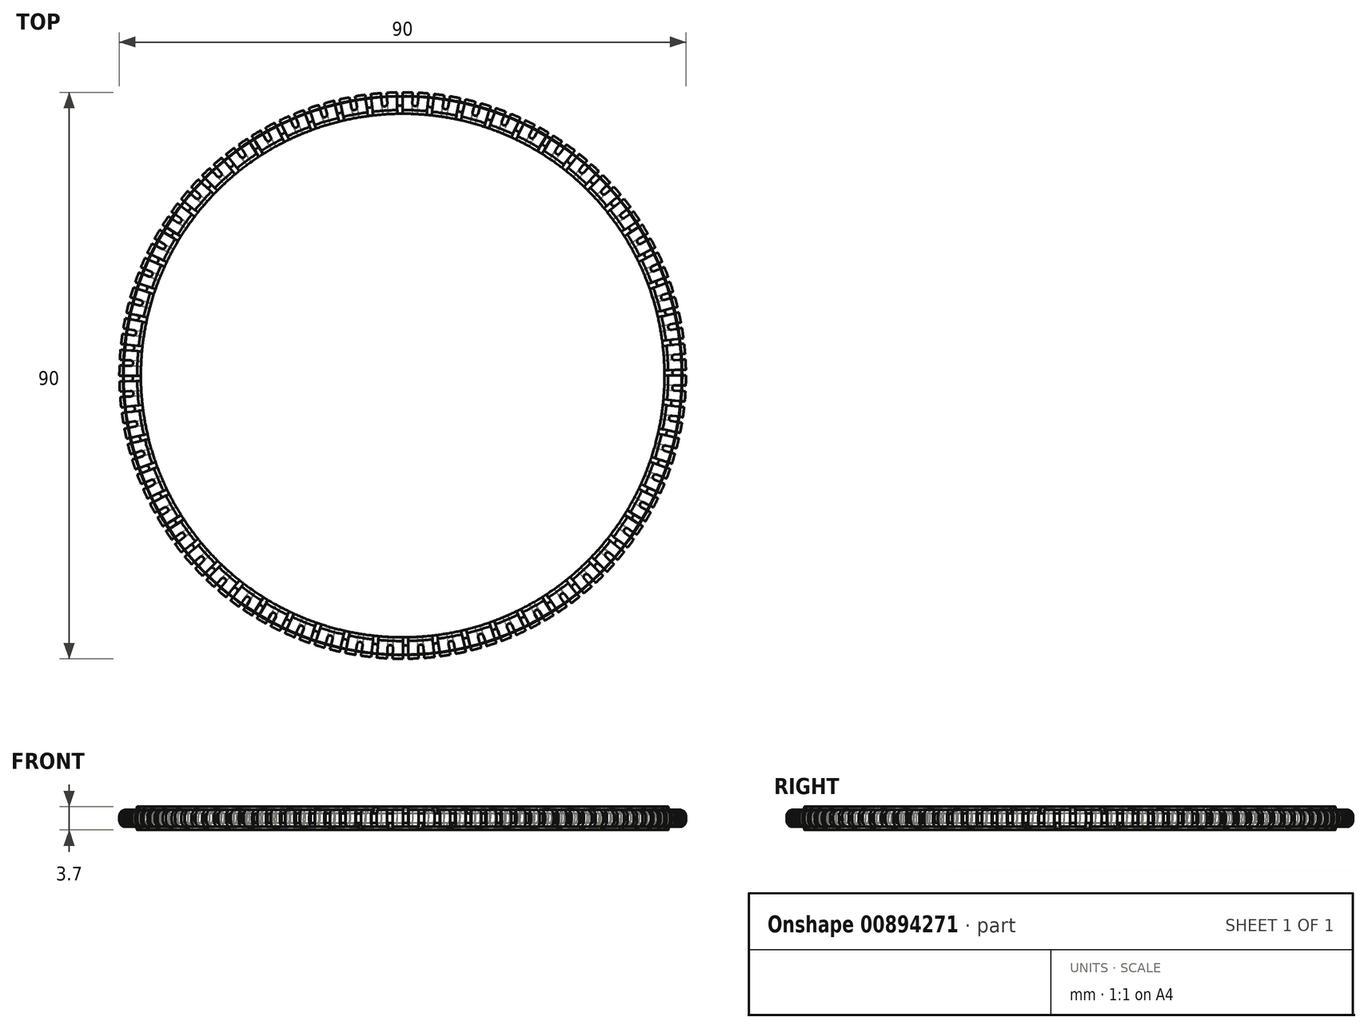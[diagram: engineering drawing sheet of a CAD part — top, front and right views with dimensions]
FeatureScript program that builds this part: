
annotation { "Feature Type Name" : "Feature", "Feature Type Description" : "" }
export const myFeature = defineFeature(function(context is Context, id is Id, definition is map)
    precondition{}
    {
        {
            var Q0;
            Q0=qCreatedBy(makeId("Right.planeOp"),FACE);
            var sketch = newSketch(context, id + "F0", { "sketchPlane" : qUnion([Q0])});
            skLineSegment(sketch, "E0", {"start": v(41.6, -1.73) * mm, "end": v(41.69, -1.3) * mm});
            skLineSegment(sketch, "E1", {"start": v(42.37, -0.75) * mm, "end": v(44, -0.75) * mm});
            skLineSegment(sketch, "E2", {"start": v(44.4, -0.35) * mm, "end": v(44.4, 0.35) * mm});
            skLineSegment(sketch, "E3", {"start": v(44, 0.75) * mm, "end": v(42.37, 0.75) * mm});
            skLineSegment(sketch, "E4", {"start": v(41.69, 1.3) * mm, "end": v(41.6, 1.73) * mm});
            skLineSegment(sketch, "E5", {"start": v(41.6, 1.73) * mm, "end": v(42.19, 1.85) * mm});
            skLineSegment(sketch, "E6", {"start": v(42.19, 1.85) * mm, "end": v(42.28, 1.43) * mm});
            skLineSegment(sketch, "E7", {"start": v(42.37, 1.35) * mm, "end": v(44, 1.35) * mm});
            skLineSegment(sketch, "E8", {"start": v(45, 0.35) * mm, "end": v(45, -0.35) * mm});
            skLineSegment(sketch, "E9", {"start": v(44, -1.35) * mm, "end": v(42.37, -1.35) * mm});
            skLineSegment(sketch, "E10", {"start": v(42.28, -1.43) * mm, "end": v(42.19, -1.85) * mm});
            skLineSegment(sketch, "E11", {"start": v(42.19, -1.85) * mm, "end": v(41.6, -1.73) * mm});
            skLineSegment(sketch, "E12", {"start": v(45, 0) * mm, "end": v(0, 0) * mm, "construction": true});
            skPoint(sketch, "E13.visualSharp", {"position": v(41.8, 0.75) * mm});
            skArc(sketch, "E13.filletArc", {"start": v(41.69, 1.3) * mm, "mid": v(41.93, 0.9) * mm, "end": v(42.37, 0.75) * mm});
            skPoint(sketch, "E14.visualSharp", {"position": v(42.3, 1.35) * mm});
            skArc(sketch, "E14.filletArc", {"start": v(42.28, 1.43) * mm, "mid": v(42.31, 1.37) * mm, "end": v(42.37, 1.35) * mm});
            skPoint(sketch, "E15.visualSharp", {"position": v(45, 1.35) * mm});
            skArc(sketch, "E15.filletArc", {"start": v(45, 0.35) * mm, "mid": v(44.7, 1.06) * mm, "end": v(44, 1.35) * mm});
            skPoint(sketch, "E16.visualSharp", {"position": v(45, -1.35) * mm});
            skArc(sketch, "E16.filletArc", {"start": v(44, -1.35) * mm, "mid": v(44.7, -1.06) * mm, "end": v(45, -0.35) * mm});
            skPoint(sketch, "E17.visualSharp", {"position": v(44.4, 0.75) * mm});
            skArc(sketch, "E17.filletArc", {"start": v(44.4, 0.35) * mm, "mid": v(44.28, 0.63) * mm, "end": v(44, 0.75) * mm});
            skPoint(sketch, "E18.visualSharp", {"position": v(44.4, -0.75) * mm});
            skArc(sketch, "E18.filletArc", {"start": v(44, -0.75) * mm, "mid": v(44.28, -0.63) * mm, "end": v(44.4, -0.35) * mm});
            skPoint(sketch, "E19.visualSharp", {"position": v(41.8, -0.75) * mm});
            skArc(sketch, "E19.filletArc", {"start": v(42.37, -0.75) * mm, "mid": v(41.93, -0.9) * mm, "end": v(41.69, -1.3) * mm});
            skPoint(sketch, "E20.visualSharp", {"position": v(42.3, -1.35) * mm});
            skArc(sketch, "E20.filletArc", {"start": v(42.37, -1.35) * mm, "mid": v(42.31, -1.37) * mm, "end": v(42.28, -1.43) * mm});
            skLineSegment(sketch, "E21", {"start": v(0, 0) * mm, "end": v(0, 20) * mm, "construction": true});
            skSolve(sketch);
        }
        {
            var Q0;
            Q0=makeQuery(id+"F0.imprint","IMPRINT",FACE,{"disambiguationData":[TD([[makeQuery(id+"F0.imprint","IMPRINT",EDGE,{"derivedFrom":sQuery(id+"F0.wireOp",EDGE,"E0")}),-1.0]])]});
            var Q1;
            Q1=sQuery(id+"F0.wireOp",EDGE,"E21");
            revolve(context, id + "F1", {"surfaceOperationType" : NewSurfaceOperationType.NEW, "entities" : qUnion([Q0]), "axis" : qUnion([Q1]), "revolveType" : RevolveType.FULL});
        }
        {
            var Q0;
            Q0=qCreatedBy(makeId("Top.planeOp"),FACE);
            var sketch = newSketch(context, id + "F2", { "sketchPlane" : qUnion([Q0])});
            skLineSegment(sketch, "E22", {"start": v(0, 0) * mm, "end": v(1.6, 44.97) * mm});
            skLineSegment(sketch, "E23", {"start": v(0, 0) * mm, "end": v(2.5, 44.93) * mm});
            skLineSegment(sketch, "E24", {"start": v(1.6, 44.97) * mm, "end": v(2.5, 44.93) * mm});
            skLineSegment(sketch, "E25", {"start": v(0, 0) * mm, "end": v(0, 45) * mm, "construction": true});
            skLineSegment(sketch, "E26.1.0", {"start": v(0, 0) * mm, "end": v(-2.55, 44.93) * mm});
            skLineSegment(sketch, "E26.1.1", {"start": v(0, 0) * mm, "end": v(-3.45, 44.87) * mm});
            skLineSegment(sketch, "E26.1.3", {"start": v(-3.45, 44.87) * mm, "end": v(-2.55, 44.93) * mm});
            skLineSegment(sketch, "E26.2.0", {"start": v(0, 0) * mm, "end": v(-7.56, 44.36) * mm});
            skLineSegment(sketch, "E26.2.1", {"start": v(0, 0) * mm, "end": v(-8.45, 44.2) * mm});
            skLineSegment(sketch, "E26.2.3", {"start": v(-8.45, 44.2) * mm, "end": v(-7.56, 44.36) * mm});
            skLineSegment(sketch, "E26.3.0", {"start": v(0, 0) * mm, "end": v(-12.48, 43.24) * mm});
            skLineSegment(sketch, "E26.3.1", {"start": v(0, 0) * mm, "end": v(-13.34, 42.98) * mm});
            skLineSegment(sketch, "E26.3.3", {"start": v(-13.34, 42.98) * mm, "end": v(-12.48, 43.24) * mm});
            skLineSegment(sketch, "E26.4.0", {"start": v(0, 0) * mm, "end": v(-17.24, 41.57) * mm});
            skLineSegment(sketch, "E26.4.1", {"start": v(0, 0) * mm, "end": v(-18.07, 41.21) * mm});
            skLineSegment(sketch, "E26.4.3", {"start": v(-18.07, 41.21) * mm, "end": v(-17.24, 41.57) * mm});
            skLineSegment(sketch, "E26.5.0", {"start": v(0, 0) * mm, "end": v(-21.79, 39.38) * mm});
            skLineSegment(sketch, "E26.5.1", {"start": v(0, 0) * mm, "end": v(-22.57, 38.93) * mm});
            skLineSegment(sketch, "E26.5.3", {"start": v(-22.57, 38.93) * mm, "end": v(-21.79, 39.38) * mm});
            skLineSegment(sketch, "E26.6.0", {"start": v(0, 0) * mm, "end": v(-26.06, 36.69) * mm});
            skLineSegment(sketch, "E26.6.1", {"start": v(0, 0) * mm, "end": v(-26.79, 36.16) * mm});
            skLineSegment(sketch, "E26.6.3", {"start": v(-26.79, 36.16) * mm, "end": v(-26.06, 36.69) * mm});
            skLineSegment(sketch, "E26.7.0", {"start": v(0, 0) * mm, "end": v(-30, 33.54) * mm});
            skLineSegment(sketch, "E26.7.1", {"start": v(0, 0) * mm, "end": v(-30.67, 32.93) * mm});
            skLineSegment(sketch, "E26.7.3", {"start": v(-30.67, 32.93) * mm, "end": v(-30, 33.54) * mm});
            skLineSegment(sketch, "E26.8.0", {"start": v(0, 0) * mm, "end": v(-33.57, 29.97) * mm});
            skLineSegment(sketch, "E26.8.1", {"start": v(0, 0) * mm, "end": v(-34.16, 29.3) * mm});
            skLineSegment(sketch, "E26.8.3", {"start": v(-34.16, 29.3) * mm, "end": v(-33.57, 29.97) * mm});
            skLineSegment(sketch, "E26.9.0", {"start": v(0, 0) * mm, "end": v(-36.72, 26.02) * mm});
            skLineSegment(sketch, "E26.9.1", {"start": v(0, 0) * mm, "end": v(-37.23, 25.28) * mm});
            skLineSegment(sketch, "E26.9.3", {"start": v(-37.23, 25.28) * mm, "end": v(-36.72, 26.02) * mm});
            skLineSegment(sketch, "E26.10.0", {"start": v(0, 0) * mm, "end": v(-39.4, 21.75) * mm});
            skLineSegment(sketch, "E26.10.1", {"start": v(0, 0) * mm, "end": v(-39.83, 20.95) * mm});
            skLineSegment(sketch, "E26.10.3", {"start": v(-39.83, 20.95) * mm, "end": v(-39.4, 21.75) * mm});
            skLineSegment(sketch, "E26.11.0", {"start": v(0, 0) * mm, "end": v(-41.59, 17.2) * mm});
            skLineSegment(sketch, "E26.11.1", {"start": v(0, 0) * mm, "end": v(-41.92, 16.36) * mm});
            skLineSegment(sketch, "E26.11.3", {"start": v(-41.92, 16.36) * mm, "end": v(-41.59, 17.2) * mm});
            skLineSegment(sketch, "E26.12.0", {"start": v(0, 0) * mm, "end": v(-43.25, 12.43) * mm});
            skLineSegment(sketch, "E26.12.1", {"start": v(0, 0) * mm, "end": v(-43.5, 11.57) * mm});
            skLineSegment(sketch, "E26.12.3", {"start": v(-43.5, 11.57) * mm, "end": v(-43.25, 12.43) * mm});
            skLineSegment(sketch, "E26.13.0", {"start": v(0, 0) * mm, "end": v(-44.37, 7.51) * mm});
            skLineSegment(sketch, "E26.13.1", {"start": v(0, 0) * mm, "end": v(-44.51, 6.63) * mm});
            skLineSegment(sketch, "E26.13.3", {"start": v(-44.51, 6.63) * mm, "end": v(-44.37, 7.51) * mm});
            skLineSegment(sketch, "E26.14.0", {"start": v(0, 0) * mm, "end": v(-44.93, 2.5) * mm});
            skLineSegment(sketch, "E26.14.1", {"start": v(0, 0) * mm, "end": v(-44.97, 1.6) * mm});
            skLineSegment(sketch, "E26.14.3", {"start": v(-44.97, 1.6) * mm, "end": v(-44.93, 2.5) * mm});
            skLineSegment(sketch, "E26.15.0", {"start": v(0, 0) * mm, "end": v(-44.93, -2.55) * mm});
            skLineSegment(sketch, "E26.15.1", {"start": v(0, 0) * mm, "end": v(-44.87, -3.45) * mm});
            skLineSegment(sketch, "E26.15.3", {"start": v(-44.87, -3.45) * mm, "end": v(-44.93, -2.55) * mm});
            skLineSegment(sketch, "E26.16.0", {"start": v(0, 0) * mm, "end": v(-44.36, -7.56) * mm});
            skLineSegment(sketch, "E26.16.1", {"start": v(0, 0) * mm, "end": v(-44.2, -8.45) * mm});
            skLineSegment(sketch, "E26.16.3", {"start": v(-44.2, -8.45) * mm, "end": v(-44.36, -7.56) * mm});
            skLineSegment(sketch, "E26.17.0", {"start": v(0, 0) * mm, "end": v(-43.24, -12.48) * mm});
            skLineSegment(sketch, "E26.17.1", {"start": v(0, 0) * mm, "end": v(-42.98, -13.34) * mm});
            skLineSegment(sketch, "E26.17.3", {"start": v(-42.98, -13.34) * mm, "end": v(-43.24, -12.48) * mm});
            skLineSegment(sketch, "E26.18.0", {"start": v(0, 0) * mm, "end": v(-41.57, -17.24) * mm});
            skLineSegment(sketch, "E26.18.1", {"start": v(0, 0) * mm, "end": v(-41.21, -18.07) * mm});
            skLineSegment(sketch, "E26.18.3", {"start": v(-41.21, -18.07) * mm, "end": v(-41.57, -17.24) * mm});
            skLineSegment(sketch, "E26.19.0", {"start": v(0, 0) * mm, "end": v(-39.38, -21.79) * mm});
            skLineSegment(sketch, "E26.19.1", {"start": v(0, 0) * mm, "end": v(-38.93, -22.57) * mm});
            skLineSegment(sketch, "E26.19.3", {"start": v(-38.93, -22.57) * mm, "end": v(-39.38, -21.79) * mm});
            skLineSegment(sketch, "E26.20.0", {"start": v(0, 0) * mm, "end": v(-36.69, -26.06) * mm});
            skLineSegment(sketch, "E26.20.1", {"start": v(0, 0) * mm, "end": v(-36.16, -26.79) * mm});
            skLineSegment(sketch, "E26.20.3", {"start": v(-36.16, -26.79) * mm, "end": v(-36.69, -26.06) * mm});
            skLineSegment(sketch, "E26.21.0", {"start": v(0, 0) * mm, "end": v(-33.54, -30) * mm});
            skLineSegment(sketch, "E26.21.1", {"start": v(0, 0) * mm, "end": v(-32.93, -30.67) * mm});
            skLineSegment(sketch, "E26.21.3", {"start": v(-32.93, -30.67) * mm, "end": v(-33.54, -30) * mm});
            skLineSegment(sketch, "E26.22.0", {"start": v(0, 0) * mm, "end": v(-29.97, -33.57) * mm});
            skLineSegment(sketch, "E26.22.1", {"start": v(0, 0) * mm, "end": v(-29.3, -34.16) * mm});
            skLineSegment(sketch, "E26.22.3", {"start": v(-29.3, -34.16) * mm, "end": v(-29.97, -33.57) * mm});
            skLineSegment(sketch, "E26.23.0", {"start": v(0, 0) * mm, "end": v(-26.02, -36.72) * mm});
            skLineSegment(sketch, "E26.23.1", {"start": v(0, 0) * mm, "end": v(-25.28, -37.23) * mm});
            skLineSegment(sketch, "E26.23.3", {"start": v(-25.28, -37.23) * mm, "end": v(-26.02, -36.72) * mm});
            skLineSegment(sketch, "E26.24.0", {"start": v(0, 0) * mm, "end": v(-21.75, -39.4) * mm});
            skLineSegment(sketch, "E26.24.1", {"start": v(0, 0) * mm, "end": v(-20.95, -39.83) * mm});
            skLineSegment(sketch, "E26.24.3", {"start": v(-20.95, -39.83) * mm, "end": v(-21.75, -39.4) * mm});
            skLineSegment(sketch, "E26.25.0", {"start": v(0, 0) * mm, "end": v(-17.2, -41.59) * mm});
            skLineSegment(sketch, "E26.25.1", {"start": v(0, 0) * mm, "end": v(-16.36, -41.92) * mm});
            skLineSegment(sketch, "E26.25.3", {"start": v(-16.36, -41.92) * mm, "end": v(-17.2, -41.59) * mm});
            skLineSegment(sketch, "E26.26.0", {"start": v(0, 0) * mm, "end": v(-12.43, -43.25) * mm});
            skLineSegment(sketch, "E26.26.1", {"start": v(0, 0) * mm, "end": v(-11.57, -43.5) * mm});
            skLineSegment(sketch, "E26.26.3", {"start": v(-11.57, -43.5) * mm, "end": v(-12.43, -43.25) * mm});
            skLineSegment(sketch, "E26.27.0", {"start": v(0, 0) * mm, "end": v(-7.51, -44.37) * mm});
            skLineSegment(sketch, "E26.27.1", {"start": v(0, 0) * mm, "end": v(-6.63, -44.51) * mm});
            skLineSegment(sketch, "E26.27.3", {"start": v(-6.63, -44.51) * mm, "end": v(-7.51, -44.37) * mm});
            skLineSegment(sketch, "E26.28.0", {"start": v(0, 0) * mm, "end": v(-2.5, -44.93) * mm});
            skLineSegment(sketch, "E26.28.1", {"start": v(0, 0) * mm, "end": v(-1.6, -44.97) * mm});
            skLineSegment(sketch, "E26.28.3", {"start": v(-1.6, -44.97) * mm, "end": v(-2.5, -44.93) * mm});
            skLineSegment(sketch, "E26.29.0", {"start": v(0, 0) * mm, "end": v(2.55, -44.93) * mm});
            skLineSegment(sketch, "E26.29.1", {"start": v(0, 0) * mm, "end": v(3.45, -44.87) * mm});
            skLineSegment(sketch, "E26.29.3", {"start": v(3.45, -44.87) * mm, "end": v(2.55, -44.93) * mm});
            skLineSegment(sketch, "E26.30.0", {"start": v(0, 0) * mm, "end": v(7.56, -44.36) * mm});
            skLineSegment(sketch, "E26.30.1", {"start": v(0, 0) * mm, "end": v(8.45, -44.2) * mm});
            skLineSegment(sketch, "E26.30.3", {"start": v(8.45, -44.2) * mm, "end": v(7.56, -44.36) * mm});
            skLineSegment(sketch, "E26.31.0", {"start": v(0, 0) * mm, "end": v(12.48, -43.24) * mm});
            skLineSegment(sketch, "E26.31.1", {"start": v(0, 0) * mm, "end": v(13.34, -42.98) * mm});
            skLineSegment(sketch, "E26.31.3", {"start": v(13.34, -42.98) * mm, "end": v(12.48, -43.24) * mm});
            skLineSegment(sketch, "E26.32.0", {"start": v(0, 0) * mm, "end": v(17.24, -41.57) * mm});
            skLineSegment(sketch, "E26.32.1", {"start": v(0, 0) * mm, "end": v(18.07, -41.21) * mm});
            skLineSegment(sketch, "E26.32.3", {"start": v(18.07, -41.21) * mm, "end": v(17.24, -41.57) * mm});
            skLineSegment(sketch, "E26.33.0", {"start": v(0, 0) * mm, "end": v(21.79, -39.38) * mm});
            skLineSegment(sketch, "E26.33.1", {"start": v(0, 0) * mm, "end": v(22.57, -38.93) * mm});
            skLineSegment(sketch, "E26.33.3", {"start": v(22.57, -38.93) * mm, "end": v(21.79, -39.38) * mm});
            skLineSegment(sketch, "E26.34.0", {"start": v(0, 0) * mm, "end": v(26.06, -36.69) * mm});
            skLineSegment(sketch, "E26.34.1", {"start": v(0, 0) * mm, "end": v(26.79, -36.16) * mm});
            skLineSegment(sketch, "E26.34.3", {"start": v(26.79, -36.16) * mm, "end": v(26.06, -36.69) * mm});
            skLineSegment(sketch, "E26.35.0", {"start": v(0, 0) * mm, "end": v(30, -33.54) * mm});
            skLineSegment(sketch, "E26.35.1", {"start": v(0, 0) * mm, "end": v(30.67, -32.93) * mm});
            skLineSegment(sketch, "E26.35.3", {"start": v(30.67, -32.93) * mm, "end": v(30, -33.54) * mm});
            skLineSegment(sketch, "E26.36.0", {"start": v(0, 0) * mm, "end": v(33.57, -29.97) * mm});
            skLineSegment(sketch, "E26.36.1", {"start": v(0, 0) * mm, "end": v(34.16, -29.3) * mm});
            skLineSegment(sketch, "E26.36.3", {"start": v(34.16, -29.3) * mm, "end": v(33.57, -29.97) * mm});
            skLineSegment(sketch, "E26.37.0", {"start": v(0, 0) * mm, "end": v(36.72, -26.02) * mm});
            skLineSegment(sketch, "E26.37.1", {"start": v(0, 0) * mm, "end": v(37.23, -25.28) * mm});
            skLineSegment(sketch, "E26.37.3", {"start": v(37.23, -25.28) * mm, "end": v(36.72, -26.02) * mm});
            skLineSegment(sketch, "E26.38.0", {"start": v(0, 0) * mm, "end": v(39.4, -21.75) * mm});
            skLineSegment(sketch, "E26.38.1", {"start": v(0, 0) * mm, "end": v(39.83, -20.95) * mm});
            skLineSegment(sketch, "E26.38.3", {"start": v(39.83, -20.95) * mm, "end": v(39.4, -21.75) * mm});
            skLineSegment(sketch, "E26.39.0", {"start": v(0, 0) * mm, "end": v(41.59, -17.2) * mm});
            skLineSegment(sketch, "E26.39.1", {"start": v(0, 0) * mm, "end": v(41.92, -16.36) * mm});
            skLineSegment(sketch, "E26.39.3", {"start": v(41.92, -16.36) * mm, "end": v(41.59, -17.2) * mm});
            skLineSegment(sketch, "E26.40.0", {"start": v(0, 0) * mm, "end": v(43.25, -12.43) * mm});
            skLineSegment(sketch, "E26.40.1", {"start": v(0, 0) * mm, "end": v(43.5, -11.57) * mm});
            skLineSegment(sketch, "E26.40.3", {"start": v(43.5, -11.57) * mm, "end": v(43.25, -12.43) * mm});
            skLineSegment(sketch, "E26.41.0", {"start": v(0, 0) * mm, "end": v(44.37, -7.51) * mm});
            skLineSegment(sketch, "E26.41.1", {"start": v(0, 0) * mm, "end": v(44.51, -6.63) * mm});
            skLineSegment(sketch, "E26.41.3", {"start": v(44.51, -6.63) * mm, "end": v(44.37, -7.51) * mm});
            skLineSegment(sketch, "E26.42.0", {"start": v(0, 0) * mm, "end": v(44.93, -2.5) * mm});
            skLineSegment(sketch, "E26.42.1", {"start": v(0, 0) * mm, "end": v(44.97, -1.6) * mm});
            skLineSegment(sketch, "E26.42.3", {"start": v(44.97, -1.6) * mm, "end": v(44.93, -2.5) * mm});
            skLineSegment(sketch, "E26.43.0", {"start": v(0, 0) * mm, "end": v(44.93, 2.55) * mm});
            skLineSegment(sketch, "E26.43.1", {"start": v(0, 0) * mm, "end": v(44.87, 3.45) * mm});
            skLineSegment(sketch, "E26.43.3", {"start": v(44.87, 3.45) * mm, "end": v(44.93, 2.55) * mm});
            skLineSegment(sketch, "E26.44.0", {"start": v(0, 0) * mm, "end": v(44.36, 7.56) * mm});
            skLineSegment(sketch, "E26.44.1", {"start": v(0, 0) * mm, "end": v(44.2, 8.45) * mm});
            skLineSegment(sketch, "E26.44.3", {"start": v(44.2, 8.45) * mm, "end": v(44.36, 7.56) * mm});
            skLineSegment(sketch, "E26.45.0", {"start": v(0, 0) * mm, "end": v(43.24, 12.48) * mm});
            skLineSegment(sketch, "E26.45.1", {"start": v(0, 0) * mm, "end": v(42.98, 13.34) * mm});
            skLineSegment(sketch, "E26.45.3", {"start": v(42.98, 13.34) * mm, "end": v(43.24, 12.48) * mm});
            skLineSegment(sketch, "E26.46.0", {"start": v(0, 0) * mm, "end": v(41.57, 17.24) * mm});
            skLineSegment(sketch, "E26.46.1", {"start": v(0, 0) * mm, "end": v(41.21, 18.07) * mm});
            skLineSegment(sketch, "E26.46.3", {"start": v(41.21, 18.07) * mm, "end": v(41.57, 17.24) * mm});
            skLineSegment(sketch, "E26.47.0", {"start": v(0, 0) * mm, "end": v(39.38, 21.79) * mm});
            skLineSegment(sketch, "E26.47.1", {"start": v(0, 0) * mm, "end": v(38.93, 22.57) * mm});
            skLineSegment(sketch, "E26.47.3", {"start": v(38.93, 22.57) * mm, "end": v(39.38, 21.79) * mm});
            skLineSegment(sketch, "E26.48.0", {"start": v(0, 0) * mm, "end": v(36.69, 26.06) * mm});
            skLineSegment(sketch, "E26.48.1", {"start": v(0, 0) * mm, "end": v(36.16, 26.79) * mm});
            skLineSegment(sketch, "E26.48.3", {"start": v(36.16, 26.79) * mm, "end": v(36.69, 26.06) * mm});
            skLineSegment(sketch, "E26.49.0", {"start": v(0, 0) * mm, "end": v(33.54, 30) * mm});
            skLineSegment(sketch, "E26.49.1", {"start": v(0, 0) * mm, "end": v(32.93, 30.67) * mm});
            skLineSegment(sketch, "E26.49.3", {"start": v(32.93, 30.67) * mm, "end": v(33.54, 30) * mm});
            skLineSegment(sketch, "E26.50.0", {"start": v(0, 0) * mm, "end": v(29.97, 33.57) * mm});
            skLineSegment(sketch, "E26.50.1", {"start": v(0, 0) * mm, "end": v(29.3, 34.16) * mm});
            skLineSegment(sketch, "E26.50.3", {"start": v(29.3, 34.16) * mm, "end": v(29.97, 33.57) * mm});
            skLineSegment(sketch, "E26.51.0", {"start": v(0, 0) * mm, "end": v(26.02, 36.72) * mm});
            skLineSegment(sketch, "E26.51.1", {"start": v(0, 0) * mm, "end": v(25.28, 37.23) * mm});
            skLineSegment(sketch, "E26.51.3", {"start": v(25.28, 37.23) * mm, "end": v(26.02, 36.72) * mm});
            skLineSegment(sketch, "E26.52.0", {"start": v(0, 0) * mm, "end": v(21.75, 39.4) * mm});
            skLineSegment(sketch, "E26.52.1", {"start": v(0, 0) * mm, "end": v(20.95, 39.83) * mm});
            skLineSegment(sketch, "E26.52.3", {"start": v(20.95, 39.83) * mm, "end": v(21.75, 39.4) * mm});
            skLineSegment(sketch, "E26.53.0", {"start": v(0, 0) * mm, "end": v(17.2, 41.59) * mm});
            skLineSegment(sketch, "E26.53.1", {"start": v(0, 0) * mm, "end": v(16.36, 41.92) * mm});
            skLineSegment(sketch, "E26.53.3", {"start": v(16.36, 41.92) * mm, "end": v(17.2, 41.59) * mm});
            skLineSegment(sketch, "E26.54.0", {"start": v(0, 0) * mm, "end": v(12.43, 43.25) * mm});
            skLineSegment(sketch, "E26.54.1", {"start": v(0, 0) * mm, "end": v(11.57, 43.5) * mm});
            skLineSegment(sketch, "E26.54.3", {"start": v(11.57, 43.5) * mm, "end": v(12.43, 43.25) * mm});
            skLineSegment(sketch, "E26.55.0", {"start": v(0, 0) * mm, "end": v(7.51, 44.37) * mm});
            skLineSegment(sketch, "E26.55.1", {"start": v(0, 0) * mm, "end": v(6.63, 44.51) * mm});
            skLineSegment(sketch, "E26.55.3", {"start": v(6.63, 44.51) * mm, "end": v(7.51, 44.37) * mm});
            skPoint(sketch, "E26.center", {"position": v(0, 0) * mm});
            skLineSegment(sketch, "E27", {"start": v(0, 0) * mm, "end": v(3.96, 43.12) * mm, "construction": true});
            skLineSegment(sketch, "E28", {"start": v(0, 0) * mm, "end": v(4.83, 43.03) * mm, "construction": true});
            skLineSegment(sketch, "E29", {"start": v(3.96, 43.12) * mm, "end": v(4.83, 43.03) * mm, "construction": true});
            skLineSegment(sketch, "E30", {"start": v(3.96, 43.12) * mm, "end": v(4.12, 44.81) * mm});
            skLineSegment(sketch, "E31", {"start": v(4.83, 43.03) * mm, "end": v(5.01, 44.72) * mm});
            skLineSegment(sketch, "E32", {"start": v(4.12, 44.81) * mm, "end": v(5.01, 44.72) * mm});
            skArc(sketch, "E33", {"start": v(3.96, 43.12) * mm, "mid": v(4.35, 42.65) * mm, "end": v(4.83, 43.03) * mm});
            skLineSegment(sketch, "E34.1.0", {"start": v(-0.89, 43.3) * mm, "end": v(-0.92, 45) * mm});
            skLineSegment(sketch, "E34.1.1", {"start": v(-0.02, 43.3) * mm, "end": v(-0.02, 45) * mm});
            skLineSegment(sketch, "E34.1.2", {"start": v(-0.92, 45) * mm, "end": v(-0.02, 45) * mm});
            skArc(sketch, "E34.1.3", {"start": v(-0.89, 43.3) * mm, "mid": v(-0.45, 42.86) * mm, "end": v(-0.02, 43.3) * mm});
            skLineSegment(sketch, "E34.1.4", {"start": v(0, 0) * mm, "end": v(-5.04, 44.72) * mm, "construction": true});
            skLineSegment(sketch, "E34.2.0", {"start": v(-5.73, 42.92) * mm, "end": v(-5.96, 44.6) * mm});
            skLineSegment(sketch, "E34.2.1", {"start": v(-4.87, 43.03) * mm, "end": v(-5.06, 44.72) * mm});
            skLineSegment(sketch, "E34.2.2", {"start": v(-5.96, 44.6) * mm, "end": v(-5.06, 44.72) * mm});
            skArc(sketch, "E34.2.3", {"start": v(-5.73, 42.92) * mm, "mid": v(-5.25, 42.54) * mm, "end": v(-4.87, 43.03) * mm});
            skLineSegment(sketch, "E34.2.4", {"start": v(0, 0) * mm, "end": v(-10.01, 43.87) * mm, "construction": true});
            skLineSegment(sketch, "E34.3.0", {"start": v(-10.5, 42) * mm, "end": v(-10.91, 43.66) * mm});
            skLineSegment(sketch, "E34.3.1", {"start": v(-9.66, 42.21) * mm, "end": v(-10.04, 43.87) * mm});
            skLineSegment(sketch, "E34.3.2", {"start": v(-10.91, 43.66) * mm, "end": v(-10.04, 43.87) * mm});
            skArc(sketch, "E34.3.3", {"start": v(-10.5, 42) * mm, "mid": v(-9.98, 41.69) * mm, "end": v(-9.66, 42.21) * mm});
            skLineSegment(sketch, "E34.3.4", {"start": v(0, 0) * mm, "end": v(-14.86, 42.47) * mm, "construction": true});
            skLineSegment(sketch, "E34.4.0", {"start": v(-15.14, 40.57) * mm, "end": v(-15.73, 42.16) * mm});
            skLineSegment(sketch, "E34.4.1", {"start": v(-14.32, 40.86) * mm, "end": v(-14.89, 42.47) * mm});
            skLineSegment(sketch, "E34.4.2", {"start": v(-15.73, 42.16) * mm, "end": v(-14.89, 42.47) * mm});
            skArc(sketch, "E34.4.3", {"start": v(-15.14, 40.57) * mm, "mid": v(-14.58, 40.3) * mm, "end": v(-14.32, 40.86) * mm});
            skLineSegment(sketch, "E34.4.4", {"start": v(0, 0) * mm, "end": v(-19.52, 40.54) * mm, "construction": true});
            skLineSegment(sketch, "E34.5.0", {"start": v(-19.59, 38.62) * mm, "end": v(-20.35, 40.14) * mm});
            skLineSegment(sketch, "E34.5.1", {"start": v(-18.8, 39) * mm, "end": v(-19.55, 40.54) * mm});
            skLineSegment(sketch, "E34.5.2", {"start": v(-20.35, 40.14) * mm, "end": v(-19.55, 40.54) * mm});
            skArc(sketch, "E34.5.3", {"start": v(-19.59, 38.62) * mm, "mid": v(-19, 38.42) * mm, "end": v(-18.8, 39) * mm});
            skLineSegment(sketch, "E34.5.4", {"start": v(0, 0) * mm, "end": v(-23.94, 38.1) * mm, "construction": true});
            skLineSegment(sketch, "E34.6.0", {"start": v(-23.79, 36.18) * mm, "end": v(-24.72, 37.6) * mm});
            skLineSegment(sketch, "E34.6.1", {"start": v(-23.06, 36.65) * mm, "end": v(-23.96, 38.1) * mm});
            skLineSegment(sketch, "E34.6.2", {"start": v(-24.72, 37.6) * mm, "end": v(-23.96, 38.1) * mm});
            skArc(sketch, "E34.6.3", {"start": v(-23.79, 36.18) * mm, "mid": v(-23.19, 36.05) * mm, "end": v(-23.06, 36.65) * mm});
            skLineSegment(sketch, "E34.6.4", {"start": v(0, 0) * mm, "end": v(-28.06, 35.18) * mm, "construction": true});
            skLineSegment(sketch, "E34.7.0", {"start": v(-27.69, 33.3) * mm, "end": v(-28.78, 34.6) * mm});
            skLineSegment(sketch, "E34.7.1", {"start": v(-27.02, 33.84) * mm, "end": v(-28.08, 35.17) * mm});
            skLineSegment(sketch, "E34.7.2", {"start": v(-28.78, 34.6) * mm, "end": v(-28.08, 35.17) * mm});
            skArc(sketch, "E34.7.3", {"start": v(-27.69, 33.3) * mm, "mid": v(-27.08, 33.23) * mm, "end": v(-27.02, 33.84) * mm});
            skLineSegment(sketch, "E34.7.4", {"start": v(0, 0) * mm, "end": v(-31.82, 31.82) * mm, "construction": true});
            skLineSegment(sketch, "E34.8.0", {"start": v(-31.24, 29.98) * mm, "end": v(-32.47, 31.16) * mm});
            skLineSegment(sketch, "E34.8.1", {"start": v(-30.64, 30.6) * mm, "end": v(-31.84, 31.8) * mm});
            skLineSegment(sketch, "E34.8.2", {"start": v(-32.47, 31.16) * mm, "end": v(-31.84, 31.8) * mm});
            skArc(sketch, "E34.8.3", {"start": v(-31.24, 29.98) * mm, "mid": v(-30.63, 30) * mm, "end": v(-30.64, 30.6) * mm});
            skLineSegment(sketch, "E34.8.4", {"start": v(0, 0) * mm, "end": v(-35.18, 28.06) * mm, "construction": true});
            skLineSegment(sketch, "E34.9.0", {"start": v(-34.4, 26.3) * mm, "end": v(-35.75, 27.33) * mm});
            skLineSegment(sketch, "E34.9.1", {"start": v(-33.87, 26.98) * mm, "end": v(-35.2, 28.04) * mm});
            skLineSegment(sketch, "E34.9.2", {"start": v(-35.75, 27.33) * mm, "end": v(-35.2, 28.04) * mm});
            skArc(sketch, "E34.9.3", {"start": v(-34.4, 26.3) * mm, "mid": v(-33.8, 26.37) * mm, "end": v(-33.87, 26.98) * mm});
            skLineSegment(sketch, "E34.9.4", {"start": v(0, 0) * mm, "end": v(-38.1, 23.94) * mm, "construction": true});
            skLineSegment(sketch, "E34.10.0", {"start": v(-37.13, 22.28) * mm, "end": v(-38.59, 23.16) * mm});
            skLineSegment(sketch, "E34.10.1", {"start": v(-36.68, 23.02) * mm, "end": v(-38.12, 23.92) * mm});
            skLineSegment(sketch, "E34.10.2", {"start": v(-38.59, 23.16) * mm, "end": v(-38.12, 23.92) * mm});
            skArc(sketch, "E34.10.3", {"start": v(-37.13, 22.28) * mm, "mid": v(-36.53, 22.42) * mm, "end": v(-36.68, 23.02) * mm});
            skLineSegment(sketch, "E34.10.4", {"start": v(0, 0) * mm, "end": v(-40.54, 19.52) * mm, "construction": true});
            skLineSegment(sketch, "E34.11.0", {"start": v(-39.4, 17.98) * mm, "end": v(-40.94, 18.69) * mm});
            skLineSegment(sketch, "E34.11.1", {"start": v(-39.02, 18.77) * mm, "end": v(-40.56, 19.5) * mm});
            skLineSegment(sketch, "E34.11.2", {"start": v(-40.94, 18.69) * mm, "end": v(-40.56, 19.5) * mm});
            skArc(sketch, "E34.11.3", {"start": v(-39.4, 17.98) * mm, "mid": v(-38.82, 18.2) * mm, "end": v(-39.02, 18.77) * mm});
            skLineSegment(sketch, "E34.11.4", {"start": v(0, 0) * mm, "end": v(-42.47, 14.86) * mm, "construction": true});
            skLineSegment(sketch, "E34.12.0", {"start": v(-41.16, 13.46) * mm, "end": v(-42.77, 13.99) * mm});
            skLineSegment(sketch, "E34.12.1", {"start": v(-40.88, 14.28) * mm, "end": v(-42.48, 14.84) * mm});
            skLineSegment(sketch, "E34.12.2", {"start": v(-42.77, 13.99) * mm, "end": v(-42.48, 14.84) * mm});
            skArc(sketch, "E34.12.3", {"start": v(-41.16, 13.46) * mm, "mid": v(-40.6, 13.73) * mm, "end": v(-40.88, 14.28) * mm});
            skLineSegment(sketch, "E34.12.4", {"start": v(0, 0) * mm, "end": v(-43.87, 10.01) * mm, "construction": true});
            skLineSegment(sketch, "E34.13.0", {"start": v(-42.4, 8.77) * mm, "end": v(-44.07, 9.11) * mm});
            skLineSegment(sketch, "E34.13.1", {"start": v(-42.22, 9.61) * mm, "end": v(-43.88, 10) * mm});
            skLineSegment(sketch, "E34.13.2", {"start": v(-44.07, 9.11) * mm, "end": v(-43.88, 10) * mm});
            skArc(sketch, "E34.13.3", {"start": v(-42.4, 8.77) * mm, "mid": v(-41.9, 9.1) * mm, "end": v(-42.22, 9.61) * mm});
            skLineSegment(sketch, "E34.13.4", {"start": v(0, 0) * mm, "end": v(-44.72, 5.04) * mm, "construction": true});
            skLineSegment(sketch, "E34.14.0", {"start": v(-43.12, 3.96) * mm, "end": v(-44.81, 4.12) * mm});
            skLineSegment(sketch, "E34.14.1", {"start": v(-43.03, 4.83) * mm, "end": v(-44.72, 5.01) * mm});
            skLineSegment(sketch, "E34.14.2", {"start": v(-44.81, 4.12) * mm, "end": v(-44.72, 5.01) * mm});
            skArc(sketch, "E34.14.3", {"start": v(-43.12, 3.96) * mm, "mid": v(-42.65, 4.35) * mm, "end": v(-43.03, 4.83) * mm});
            skLineSegment(sketch, "E34.14.4", {"start": v(0, 0) * mm, "end": v(-45, 0) * mm, "construction": true});
            skLineSegment(sketch, "E34.15.0", {"start": v(-43.3, -0.89) * mm, "end": v(-45, -0.92) * mm});
            skLineSegment(sketch, "E34.15.1", {"start": v(-43.3, -0.02) * mm, "end": v(-45, -0.02) * mm});
            skLineSegment(sketch, "E34.15.2", {"start": v(-45, -0.92) * mm, "end": v(-45, -0.02) * mm});
            skArc(sketch, "E34.15.3", {"start": v(-43.3, -0.89) * mm, "mid": v(-42.86, -0.45) * mm, "end": v(-43.3, -0.02) * mm});
            skLineSegment(sketch, "E34.15.4", {"start": v(0, 0) * mm, "end": v(-44.72, -5.04) * mm, "construction": true});
            skLineSegment(sketch, "E34.16.0", {"start": v(-42.92, -5.73) * mm, "end": v(-44.6, -5.96) * mm});
            skLineSegment(sketch, "E34.16.1", {"start": v(-43.03, -4.87) * mm, "end": v(-44.72, -5.06) * mm});
            skLineSegment(sketch, "E34.16.2", {"start": v(-44.6, -5.96) * mm, "end": v(-44.72, -5.06) * mm});
            skArc(sketch, "E34.16.3", {"start": v(-42.92, -5.73) * mm, "mid": v(-42.54, -5.25) * mm, "end": v(-43.03, -4.87) * mm});
            skLineSegment(sketch, "E34.16.4", {"start": v(0, 0) * mm, "end": v(-43.87, -10.01) * mm, "construction": true});
            skLineSegment(sketch, "E34.17.0", {"start": v(-42, -10.5) * mm, "end": v(-43.66, -10.91) * mm});
            skLineSegment(sketch, "E34.17.1", {"start": v(-42.21, -9.66) * mm, "end": v(-43.87, -10.04) * mm});
            skLineSegment(sketch, "E34.17.2", {"start": v(-43.66, -10.91) * mm, "end": v(-43.87, -10.04) * mm});
            skArc(sketch, "E34.17.3", {"start": v(-42, -10.5) * mm, "mid": v(-41.69, -9.98) * mm, "end": v(-42.21, -9.66) * mm});
            skLineSegment(sketch, "E34.17.4", {"start": v(0, 0) * mm, "end": v(-42.47, -14.86) * mm, "construction": true});
            skLineSegment(sketch, "E34.18.0", {"start": v(-40.57, -15.14) * mm, "end": v(-42.16, -15.73) * mm});
            skLineSegment(sketch, "E34.18.1", {"start": v(-40.86, -14.32) * mm, "end": v(-42.47, -14.89) * mm});
            skLineSegment(sketch, "E34.18.2", {"start": v(-42.16, -15.73) * mm, "end": v(-42.47, -14.89) * mm});
            skArc(sketch, "E34.18.3", {"start": v(-40.57, -15.14) * mm, "mid": v(-40.3, -14.58) * mm, "end": v(-40.86, -14.32) * mm});
            skLineSegment(sketch, "E34.18.4", {"start": v(0, 0) * mm, "end": v(-40.54, -19.52) * mm, "construction": true});
            skLineSegment(sketch, "E34.19.0", {"start": v(-38.62, -19.59) * mm, "end": v(-40.14, -20.35) * mm});
            skLineSegment(sketch, "E34.19.1", {"start": v(-39, -18.8) * mm, "end": v(-40.54, -19.55) * mm});
            skLineSegment(sketch, "E34.19.2", {"start": v(-40.14, -20.35) * mm, "end": v(-40.54, -19.55) * mm});
            skArc(sketch, "E34.19.3", {"start": v(-38.62, -19.59) * mm, "mid": v(-38.42, -19) * mm, "end": v(-39, -18.8) * mm});
            skLineSegment(sketch, "E34.19.4", {"start": v(0, 0) * mm, "end": v(-38.1, -23.94) * mm, "construction": true});
            skLineSegment(sketch, "E34.20.0", {"start": v(-36.18, -23.79) * mm, "end": v(-37.6, -24.72) * mm});
            skLineSegment(sketch, "E34.20.1", {"start": v(-36.65, -23.06) * mm, "end": v(-38.1, -23.96) * mm});
            skLineSegment(sketch, "E34.20.2", {"start": v(-37.6, -24.72) * mm, "end": v(-38.1, -23.96) * mm});
            skArc(sketch, "E34.20.3", {"start": v(-36.18, -23.79) * mm, "mid": v(-36.05, -23.19) * mm, "end": v(-36.65, -23.06) * mm});
            skLineSegment(sketch, "E34.20.4", {"start": v(0, 0) * mm, "end": v(-35.18, -28.06) * mm, "construction": true});
            skLineSegment(sketch, "E34.21.0", {"start": v(-33.3, -27.69) * mm, "end": v(-34.6, -28.78) * mm});
            skLineSegment(sketch, "E34.21.1", {"start": v(-33.84, -27.02) * mm, "end": v(-35.17, -28.08) * mm});
            skLineSegment(sketch, "E34.21.2", {"start": v(-34.6, -28.78) * mm, "end": v(-35.17, -28.08) * mm});
            skArc(sketch, "E34.21.3", {"start": v(-33.3, -27.69) * mm, "mid": v(-33.23, -27.08) * mm, "end": v(-33.84, -27.02) * mm});
            skLineSegment(sketch, "E34.21.4", {"start": v(0, 0) * mm, "end": v(-31.82, -31.82) * mm, "construction": true});
            skLineSegment(sketch, "E34.22.0", {"start": v(-29.98, -31.24) * mm, "end": v(-31.16, -32.47) * mm});
            skLineSegment(sketch, "E34.22.1", {"start": v(-30.6, -30.64) * mm, "end": v(-31.8, -31.84) * mm});
            skLineSegment(sketch, "E34.22.2", {"start": v(-31.16, -32.47) * mm, "end": v(-31.8, -31.84) * mm});
            skArc(sketch, "E34.22.3", {"start": v(-29.98, -31.24) * mm, "mid": v(-30, -30.63) * mm, "end": v(-30.6, -30.64) * mm});
            skLineSegment(sketch, "E34.22.4", {"start": v(0, 0) * mm, "end": v(-28.06, -35.18) * mm, "construction": true});
            skLineSegment(sketch, "E34.23.0", {"start": v(-26.3, -34.4) * mm, "end": v(-27.33, -35.75) * mm});
            skLineSegment(sketch, "E34.23.1", {"start": v(-26.98, -33.87) * mm, "end": v(-28.04, -35.2) * mm});
            skLineSegment(sketch, "E34.23.2", {"start": v(-27.33, -35.75) * mm, "end": v(-28.04, -35.2) * mm});
            skArc(sketch, "E34.23.3", {"start": v(-26.3, -34.4) * mm, "mid": v(-26.37, -33.8) * mm, "end": v(-26.98, -33.87) * mm});
            skLineSegment(sketch, "E34.23.4", {"start": v(0, 0) * mm, "end": v(-23.94, -38.1) * mm, "construction": true});
            skLineSegment(sketch, "E34.24.0", {"start": v(-22.28, -37.13) * mm, "end": v(-23.16, -38.59) * mm});
            skLineSegment(sketch, "E34.24.1", {"start": v(-23.02, -36.68) * mm, "end": v(-23.92, -38.12) * mm});
            skLineSegment(sketch, "E34.24.2", {"start": v(-23.16, -38.59) * mm, "end": v(-23.92, -38.12) * mm});
            skArc(sketch, "E34.24.3", {"start": v(-22.28, -37.13) * mm, "mid": v(-22.42, -36.53) * mm, "end": v(-23.02, -36.68) * mm});
            skLineSegment(sketch, "E34.24.4", {"start": v(0, 0) * mm, "end": v(-19.52, -40.54) * mm, "construction": true});
            skLineSegment(sketch, "E34.25.0", {"start": v(-17.98, -39.4) * mm, "end": v(-18.69, -40.94) * mm});
            skLineSegment(sketch, "E34.25.1", {"start": v(-18.77, -39.02) * mm, "end": v(-19.5, -40.56) * mm});
            skLineSegment(sketch, "E34.25.2", {"start": v(-18.69, -40.94) * mm, "end": v(-19.5, -40.56) * mm});
            skArc(sketch, "E34.25.3", {"start": v(-17.98, -39.4) * mm, "mid": v(-18.2, -38.82) * mm, "end": v(-18.77, -39.02) * mm});
            skLineSegment(sketch, "E34.25.4", {"start": v(0, 0) * mm, "end": v(-14.86, -42.47) * mm, "construction": true});
            skLineSegment(sketch, "E34.26.0", {"start": v(-13.46, -41.16) * mm, "end": v(-13.99, -42.77) * mm});
            skLineSegment(sketch, "E34.26.1", {"start": v(-14.28, -40.88) * mm, "end": v(-14.84, -42.48) * mm});
            skLineSegment(sketch, "E34.26.2", {"start": v(-13.99, -42.77) * mm, "end": v(-14.84, -42.48) * mm});
            skArc(sketch, "E34.26.3", {"start": v(-13.46, -41.16) * mm, "mid": v(-13.73, -40.6) * mm, "end": v(-14.28, -40.88) * mm});
            skLineSegment(sketch, "E34.26.4", {"start": v(0, 0) * mm, "end": v(-10.01, -43.87) * mm, "construction": true});
            skLineSegment(sketch, "E34.27.0", {"start": v(-8.77, -42.4) * mm, "end": v(-9.11, -44.07) * mm});
            skLineSegment(sketch, "E34.27.1", {"start": v(-9.61, -42.22) * mm, "end": v(-10, -43.88) * mm});
            skLineSegment(sketch, "E34.27.2", {"start": v(-9.11, -44.07) * mm, "end": v(-10, -43.88) * mm});
            skArc(sketch, "E34.27.3", {"start": v(-8.77, -42.4) * mm, "mid": v(-9.1, -41.9) * mm, "end": v(-9.61, -42.22) * mm});
            skLineSegment(sketch, "E34.27.4", {"start": v(0, 0) * mm, "end": v(-5.04, -44.72) * mm, "construction": true});
            skLineSegment(sketch, "E34.28.0", {"start": v(-3.96, -43.12) * mm, "end": v(-4.12, -44.81) * mm});
            skLineSegment(sketch, "E34.28.1", {"start": v(-4.83, -43.03) * mm, "end": v(-5.01, -44.72) * mm});
            skLineSegment(sketch, "E34.28.2", {"start": v(-4.12, -44.81) * mm, "end": v(-5.01, -44.72) * mm});
            skArc(sketch, "E34.28.3", {"start": v(-3.96, -43.12) * mm, "mid": v(-4.35, -42.65) * mm, "end": v(-4.83, -43.03) * mm});
            skLineSegment(sketch, "E34.28.4", {"start": v(0, 0) * mm, "end": v(0, -45) * mm, "construction": true});
            skLineSegment(sketch, "E34.29.0", {"start": v(0.89, -43.3) * mm, "end": v(0.92, -45) * mm});
            skLineSegment(sketch, "E34.29.1", {"start": v(0.02, -43.3) * mm, "end": v(0.02, -45) * mm});
            skLineSegment(sketch, "E34.29.2", {"start": v(0.92, -45) * mm, "end": v(0.02, -45) * mm});
            skArc(sketch, "E34.29.3", {"start": v(0.89, -43.3) * mm, "mid": v(0.45, -42.86) * mm, "end": v(0.02, -43.3) * mm});
            skLineSegment(sketch, "E34.29.4", {"start": v(0, 0) * mm, "end": v(5.04, -44.72) * mm, "construction": true});
            skLineSegment(sketch, "E34.30.0", {"start": v(5.73, -42.92) * mm, "end": v(5.96, -44.6) * mm});
            skLineSegment(sketch, "E34.30.1", {"start": v(4.87, -43.03) * mm, "end": v(5.06, -44.72) * mm});
            skLineSegment(sketch, "E34.30.2", {"start": v(5.96, -44.6) * mm, "end": v(5.06, -44.72) * mm});
            skArc(sketch, "E34.30.3", {"start": v(5.73, -42.92) * mm, "mid": v(5.25, -42.54) * mm, "end": v(4.87, -43.03) * mm});
            skLineSegment(sketch, "E34.30.4", {"start": v(0, 0) * mm, "end": v(10.01, -43.87) * mm, "construction": true});
            skLineSegment(sketch, "E34.31.0", {"start": v(10.5, -42) * mm, "end": v(10.91, -43.66) * mm});
            skLineSegment(sketch, "E34.31.1", {"start": v(9.66, -42.21) * mm, "end": v(10.04, -43.87) * mm});
            skLineSegment(sketch, "E34.31.2", {"start": v(10.91, -43.66) * mm, "end": v(10.04, -43.87) * mm});
            skArc(sketch, "E34.31.3", {"start": v(10.5, -42) * mm, "mid": v(9.98, -41.69) * mm, "end": v(9.66, -42.21) * mm});
            skLineSegment(sketch, "E34.31.4", {"start": v(0, 0) * mm, "end": v(14.86, -42.47) * mm, "construction": true});
            skLineSegment(sketch, "E34.32.0", {"start": v(15.14, -40.57) * mm, "end": v(15.73, -42.16) * mm});
            skLineSegment(sketch, "E34.32.1", {"start": v(14.32, -40.86) * mm, "end": v(14.89, -42.47) * mm});
            skLineSegment(sketch, "E34.32.2", {"start": v(15.73, -42.16) * mm, "end": v(14.89, -42.47) * mm});
            skArc(sketch, "E34.32.3", {"start": v(15.14, -40.57) * mm, "mid": v(14.58, -40.3) * mm, "end": v(14.32, -40.86) * mm});
            skLineSegment(sketch, "E34.32.4", {"start": v(0, 0) * mm, "end": v(19.52, -40.54) * mm, "construction": true});
            skLineSegment(sketch, "E34.33.0", {"start": v(19.59, -38.62) * mm, "end": v(20.35, -40.14) * mm});
            skLineSegment(sketch, "E34.33.1", {"start": v(18.8, -39) * mm, "end": v(19.55, -40.54) * mm});
            skLineSegment(sketch, "E34.33.2", {"start": v(20.35, -40.14) * mm, "end": v(19.55, -40.54) * mm});
            skArc(sketch, "E34.33.3", {"start": v(19.59, -38.62) * mm, "mid": v(19, -38.42) * mm, "end": v(18.8, -39) * mm});
            skLineSegment(sketch, "E34.33.4", {"start": v(0, 0) * mm, "end": v(23.94, -38.1) * mm, "construction": true});
            skLineSegment(sketch, "E34.34.0", {"start": v(23.79, -36.18) * mm, "end": v(24.72, -37.6) * mm});
            skLineSegment(sketch, "E34.34.1", {"start": v(23.06, -36.65) * mm, "end": v(23.96, -38.1) * mm});
            skLineSegment(sketch, "E34.34.2", {"start": v(24.72, -37.6) * mm, "end": v(23.96, -38.1) * mm});
            skArc(sketch, "E34.34.3", {"start": v(23.79, -36.18) * mm, "mid": v(23.19, -36.05) * mm, "end": v(23.06, -36.65) * mm});
            skLineSegment(sketch, "E34.34.4", {"start": v(0, 0) * mm, "end": v(28.06, -35.18) * mm, "construction": true});
            skLineSegment(sketch, "E34.35.0", {"start": v(27.69, -33.3) * mm, "end": v(28.78, -34.6) * mm});
            skLineSegment(sketch, "E34.35.1", {"start": v(27.02, -33.84) * mm, "end": v(28.08, -35.17) * mm});
            skLineSegment(sketch, "E34.35.2", {"start": v(28.78, -34.6) * mm, "end": v(28.08, -35.17) * mm});
            skArc(sketch, "E34.35.3", {"start": v(27.69, -33.3) * mm, "mid": v(27.08, -33.23) * mm, "end": v(27.02, -33.84) * mm});
            skLineSegment(sketch, "E34.35.4", {"start": v(0, 0) * mm, "end": v(31.82, -31.82) * mm, "construction": true});
            skLineSegment(sketch, "E34.36.0", {"start": v(31.24, -29.98) * mm, "end": v(32.47, -31.16) * mm});
            skLineSegment(sketch, "E34.36.1", {"start": v(30.64, -30.6) * mm, "end": v(31.84, -31.8) * mm});
            skLineSegment(sketch, "E34.36.2", {"start": v(32.47, -31.16) * mm, "end": v(31.84, -31.8) * mm});
            skArc(sketch, "E34.36.3", {"start": v(31.24, -29.98) * mm, "mid": v(30.63, -30) * mm, "end": v(30.64, -30.6) * mm});
            skLineSegment(sketch, "E34.36.4", {"start": v(0, 0) * mm, "end": v(35.18, -28.06) * mm, "construction": true});
            skLineSegment(sketch, "E34.37.0", {"start": v(34.4, -26.3) * mm, "end": v(35.75, -27.33) * mm});
            skLineSegment(sketch, "E34.37.1", {"start": v(33.87, -26.98) * mm, "end": v(35.2, -28.04) * mm});
            skLineSegment(sketch, "E34.37.2", {"start": v(35.75, -27.33) * mm, "end": v(35.2, -28.04) * mm});
            skArc(sketch, "E34.37.3", {"start": v(34.4, -26.3) * mm, "mid": v(33.8, -26.37) * mm, "end": v(33.87, -26.98) * mm});
            skLineSegment(sketch, "E34.37.4", {"start": v(0, 0) * mm, "end": v(38.1, -23.94) * mm, "construction": true});
            skLineSegment(sketch, "E34.38.0", {"start": v(37.13, -22.28) * mm, "end": v(38.59, -23.16) * mm});
            skLineSegment(sketch, "E34.38.1", {"start": v(36.68, -23.02) * mm, "end": v(38.12, -23.92) * mm});
            skLineSegment(sketch, "E34.38.2", {"start": v(38.59, -23.16) * mm, "end": v(38.12, -23.92) * mm});
            skArc(sketch, "E34.38.3", {"start": v(37.13, -22.28) * mm, "mid": v(36.53, -22.42) * mm, "end": v(36.68, -23.02) * mm});
            skLineSegment(sketch, "E34.38.4", {"start": v(0, 0) * mm, "end": v(40.54, -19.52) * mm, "construction": true});
            skLineSegment(sketch, "E34.39.0", {"start": v(39.4, -17.98) * mm, "end": v(40.94, -18.69) * mm});
            skLineSegment(sketch, "E34.39.1", {"start": v(39.02, -18.77) * mm, "end": v(40.56, -19.5) * mm});
            skLineSegment(sketch, "E34.39.2", {"start": v(40.94, -18.69) * mm, "end": v(40.56, -19.5) * mm});
            skArc(sketch, "E34.39.3", {"start": v(39.4, -17.98) * mm, "mid": v(38.82, -18.2) * mm, "end": v(39.02, -18.77) * mm});
            skLineSegment(sketch, "E34.39.4", {"start": v(0, 0) * mm, "end": v(42.47, -14.86) * mm, "construction": true});
            skLineSegment(sketch, "E34.40.0", {"start": v(41.16, -13.46) * mm, "end": v(42.77, -13.99) * mm});
            skLineSegment(sketch, "E34.40.1", {"start": v(40.88, -14.28) * mm, "end": v(42.48, -14.84) * mm});
            skLineSegment(sketch, "E34.40.2", {"start": v(42.77, -13.99) * mm, "end": v(42.48, -14.84) * mm});
            skArc(sketch, "E34.40.3", {"start": v(41.16, -13.46) * mm, "mid": v(40.6, -13.73) * mm, "end": v(40.88, -14.28) * mm});
            skLineSegment(sketch, "E34.40.4", {"start": v(0, 0) * mm, "end": v(43.87, -10.01) * mm, "construction": true});
            skLineSegment(sketch, "E34.41.0", {"start": v(42.4, -8.77) * mm, "end": v(44.07, -9.11) * mm});
            skLineSegment(sketch, "E34.41.1", {"start": v(42.22, -9.61) * mm, "end": v(43.88, -10) * mm});
            skLineSegment(sketch, "E34.41.2", {"start": v(44.07, -9.11) * mm, "end": v(43.88, -10) * mm});
            skArc(sketch, "E34.41.3", {"start": v(42.4, -8.77) * mm, "mid": v(41.9, -9.1) * mm, "end": v(42.22, -9.61) * mm});
            skLineSegment(sketch, "E34.41.4", {"start": v(0, 0) * mm, "end": v(44.72, -5.04) * mm, "construction": true});
            skLineSegment(sketch, "E34.42.0", {"start": v(43.12, -3.96) * mm, "end": v(44.81, -4.12) * mm});
            skLineSegment(sketch, "E34.42.1", {"start": v(43.03, -4.83) * mm, "end": v(44.72, -5.01) * mm});
            skLineSegment(sketch, "E34.42.2", {"start": v(44.81, -4.12) * mm, "end": v(44.72, -5.01) * mm});
            skArc(sketch, "E34.42.3", {"start": v(43.12, -3.96) * mm, "mid": v(42.65, -4.35) * mm, "end": v(43.03, -4.83) * mm});
            skLineSegment(sketch, "E34.42.4", {"start": v(0, 0) * mm, "end": v(45, 0) * mm, "construction": true});
            skLineSegment(sketch, "E34.43.0", {"start": v(43.3, 0.89) * mm, "end": v(45, 0.92) * mm});
            skLineSegment(sketch, "E34.43.1", {"start": v(43.3, 0.02) * mm, "end": v(45, 0.02) * mm});
            skLineSegment(sketch, "E34.43.2", {"start": v(45, 0.92) * mm, "end": v(45, 0.02) * mm});
            skArc(sketch, "E34.43.3", {"start": v(43.3, 0.89) * mm, "mid": v(42.86, 0.45) * mm, "end": v(43.3, 0.02) * mm});
            skLineSegment(sketch, "E34.43.4", {"start": v(0, 0) * mm, "end": v(44.72, 5.04) * mm, "construction": true});
            skLineSegment(sketch, "E34.44.0", {"start": v(42.92, 5.73) * mm, "end": v(44.6, 5.96) * mm});
            skLineSegment(sketch, "E34.44.1", {"start": v(43.03, 4.87) * mm, "end": v(44.72, 5.06) * mm});
            skLineSegment(sketch, "E34.44.2", {"start": v(44.6, 5.96) * mm, "end": v(44.72, 5.06) * mm});
            skArc(sketch, "E34.44.3", {"start": v(42.92, 5.73) * mm, "mid": v(42.54, 5.25) * mm, "end": v(43.03, 4.87) * mm});
            skLineSegment(sketch, "E34.44.4", {"start": v(0, 0) * mm, "end": v(43.87, 10.01) * mm, "construction": true});
            skLineSegment(sketch, "E34.45.0", {"start": v(42, 10.5) * mm, "end": v(43.66, 10.91) * mm});
            skLineSegment(sketch, "E34.45.1", {"start": v(42.21, 9.66) * mm, "end": v(43.87, 10.04) * mm});
            skLineSegment(sketch, "E34.45.2", {"start": v(43.66, 10.91) * mm, "end": v(43.87, 10.04) * mm});
            skArc(sketch, "E34.45.3", {"start": v(42, 10.5) * mm, "mid": v(41.69, 9.98) * mm, "end": v(42.21, 9.66) * mm});
            skLineSegment(sketch, "E34.45.4", {"start": v(0, 0) * mm, "end": v(42.47, 14.86) * mm, "construction": true});
            skLineSegment(sketch, "E34.46.0", {"start": v(40.57, 15.14) * mm, "end": v(42.16, 15.73) * mm});
            skLineSegment(sketch, "E34.46.1", {"start": v(40.86, 14.32) * mm, "end": v(42.47, 14.89) * mm});
            skLineSegment(sketch, "E34.46.2", {"start": v(42.16, 15.73) * mm, "end": v(42.47, 14.89) * mm});
            skArc(sketch, "E34.46.3", {"start": v(40.57, 15.14) * mm, "mid": v(40.3, 14.58) * mm, "end": v(40.86, 14.32) * mm});
            skLineSegment(sketch, "E34.46.4", {"start": v(0, 0) * mm, "end": v(40.54, 19.52) * mm, "construction": true});
            skLineSegment(sketch, "E34.47.0", {"start": v(38.62, 19.59) * mm, "end": v(40.14, 20.35) * mm});
            skLineSegment(sketch, "E34.47.1", {"start": v(39, 18.8) * mm, "end": v(40.54, 19.55) * mm});
            skLineSegment(sketch, "E34.47.2", {"start": v(40.14, 20.35) * mm, "end": v(40.54, 19.55) * mm});
            skArc(sketch, "E34.47.3", {"start": v(38.62, 19.59) * mm, "mid": v(38.42, 19) * mm, "end": v(39, 18.8) * mm});
            skLineSegment(sketch, "E34.47.4", {"start": v(0, 0) * mm, "end": v(38.1, 23.94) * mm, "construction": true});
            skLineSegment(sketch, "E34.48.0", {"start": v(36.18, 23.79) * mm, "end": v(37.6, 24.72) * mm});
            skLineSegment(sketch, "E34.48.1", {"start": v(36.65, 23.06) * mm, "end": v(38.1, 23.96) * mm});
            skLineSegment(sketch, "E34.48.2", {"start": v(37.6, 24.72) * mm, "end": v(38.1, 23.96) * mm});
            skArc(sketch, "E34.48.3", {"start": v(36.18, 23.79) * mm, "mid": v(36.05, 23.19) * mm, "end": v(36.65, 23.06) * mm});
            skLineSegment(sketch, "E34.48.4", {"start": v(0, 0) * mm, "end": v(35.18, 28.06) * mm, "construction": true});
            skLineSegment(sketch, "E34.49.0", {"start": v(33.3, 27.69) * mm, "end": v(34.6, 28.78) * mm});
            skLineSegment(sketch, "E34.49.1", {"start": v(33.84, 27.02) * mm, "end": v(35.17, 28.08) * mm});
            skLineSegment(sketch, "E34.49.2", {"start": v(34.6, 28.78) * mm, "end": v(35.17, 28.08) * mm});
            skArc(sketch, "E34.49.3", {"start": v(33.3, 27.69) * mm, "mid": v(33.23, 27.08) * mm, "end": v(33.84, 27.02) * mm});
            skLineSegment(sketch, "E34.49.4", {"start": v(0, 0) * mm, "end": v(31.82, 31.82) * mm, "construction": true});
            skLineSegment(sketch, "E34.50.0", {"start": v(29.98, 31.24) * mm, "end": v(31.16, 32.47) * mm});
            skLineSegment(sketch, "E34.50.1", {"start": v(30.6, 30.64) * mm, "end": v(31.8, 31.84) * mm});
            skLineSegment(sketch, "E34.50.2", {"start": v(31.16, 32.47) * mm, "end": v(31.8, 31.84) * mm});
            skArc(sketch, "E34.50.3", {"start": v(29.98, 31.24) * mm, "mid": v(30, 30.63) * mm, "end": v(30.6, 30.64) * mm});
            skLineSegment(sketch, "E34.50.4", {"start": v(0, 0) * mm, "end": v(28.06, 35.18) * mm, "construction": true});
            skLineSegment(sketch, "E34.51.0", {"start": v(26.3, 34.4) * mm, "end": v(27.33, 35.75) * mm});
            skLineSegment(sketch, "E34.51.1", {"start": v(26.98, 33.87) * mm, "end": v(28.04, 35.2) * mm});
            skLineSegment(sketch, "E34.51.2", {"start": v(27.33, 35.75) * mm, "end": v(28.04, 35.2) * mm});
            skArc(sketch, "E34.51.3", {"start": v(26.3, 34.4) * mm, "mid": v(26.37, 33.8) * mm, "end": v(26.98, 33.87) * mm});
            skLineSegment(sketch, "E34.51.4", {"start": v(0, 0) * mm, "end": v(23.94, 38.1) * mm, "construction": true});
            skLineSegment(sketch, "E34.52.0", {"start": v(22.28, 37.13) * mm, "end": v(23.16, 38.59) * mm});
            skLineSegment(sketch, "E34.52.1", {"start": v(23.02, 36.68) * mm, "end": v(23.92, 38.12) * mm});
            skLineSegment(sketch, "E34.52.2", {"start": v(23.16, 38.59) * mm, "end": v(23.92, 38.12) * mm});
            skArc(sketch, "E34.52.3", {"start": v(22.28, 37.13) * mm, "mid": v(22.42, 36.53) * mm, "end": v(23.02, 36.68) * mm});
            skLineSegment(sketch, "E34.52.4", {"start": v(0, 0) * mm, "end": v(19.52, 40.54) * mm, "construction": true});
            skLineSegment(sketch, "E34.53.0", {"start": v(17.98, 39.4) * mm, "end": v(18.69, 40.94) * mm});
            skLineSegment(sketch, "E34.53.1", {"start": v(18.77, 39.02) * mm, "end": v(19.5, 40.56) * mm});
            skLineSegment(sketch, "E34.53.2", {"start": v(18.69, 40.94) * mm, "end": v(19.5, 40.56) * mm});
            skArc(sketch, "E34.53.3", {"start": v(17.98, 39.4) * mm, "mid": v(18.2, 38.82) * mm, "end": v(18.77, 39.02) * mm});
            skLineSegment(sketch, "E34.53.4", {"start": v(0, 0) * mm, "end": v(14.86, 42.47) * mm, "construction": true});
            skLineSegment(sketch, "E34.54.0", {"start": v(13.46, 41.16) * mm, "end": v(13.99, 42.77) * mm});
            skLineSegment(sketch, "E34.54.1", {"start": v(14.28, 40.88) * mm, "end": v(14.84, 42.48) * mm});
            skLineSegment(sketch, "E34.54.2", {"start": v(13.99, 42.77) * mm, "end": v(14.84, 42.48) * mm});
            skArc(sketch, "E34.54.3", {"start": v(13.46, 41.16) * mm, "mid": v(13.73, 40.6) * mm, "end": v(14.28, 40.88) * mm});
            skLineSegment(sketch, "E34.54.4", {"start": v(0, 0) * mm, "end": v(10.01, 43.87) * mm, "construction": true});
            skLineSegment(sketch, "E34.55.0", {"start": v(8.77, 42.4) * mm, "end": v(9.11, 44.07) * mm});
            skLineSegment(sketch, "E34.55.1", {"start": v(9.61, 42.22) * mm, "end": v(10, 43.88) * mm});
            skLineSegment(sketch, "E34.55.2", {"start": v(9.11, 44.07) * mm, "end": v(10, 43.88) * mm});
            skArc(sketch, "E34.55.3", {"start": v(8.77, 42.4) * mm, "mid": v(9.1, 41.9) * mm, "end": v(9.61, 42.22) * mm});
            skLineSegment(sketch, "E34.55.4", {"start": v(0, 0) * mm, "end": v(5.04, 44.72) * mm, "construction": true});
            skSolve(sketch);
        }
        {
            var Q0;
            Q0 = qSketchRegion(id + "F2", true);
            extrude(context, id + "F3", {"entities" : qUnion([Q0]), "operationType" : NewBodyOperationType.REMOVE, "endBound" : BoundingType.THROUGH_ALL, "oppositeDirection" : true, "depth" : 25 * mm, "offsetDistance" : 25 * mm});
        }
        {
            var Q0;
            Q0=qCreatedBy(makeId("Top.planeOp"),FACE);
            var sketch = newSketch(context, id + "F4", { "sketchPlane" : qUnion([Q0])});
            skLineSegment(sketch, "E35", {"start": v(0, 0) * mm, "end": v(1.54, 43.27) * mm, "construction": true});
            skLineSegment(sketch, "E36", {"start": v(0, 0) * mm, "end": v(2.4, 43.24) * mm, "construction": true});
            skLineSegment(sketch, "E37", {"start": v(1.54, 43.27) * mm, "end": v(2.4, 43.24) * mm, "construction": true});
            skLineSegment(sketch, "E38", {"start": v(1.54, 43.27) * mm, "end": v(1.6, 44.97) * mm});
            skLineSegment(sketch, "E39", {"start": v(2.4, 43.24) * mm, "end": v(2.5, 44.93) * mm});
            skLineSegment(sketch, "E40", {"start": v(1.6, 44.97) * mm, "end": v(2.5, 44.93) * mm});
            skArc(sketch, "E41", {"start": v(1.54, 43.27) * mm, "mid": v(1.95, 42.82) * mm, "end": v(2.4, 43.24) * mm});
            skLineSegment(sketch, "E42", {"start": v(0, 0) * mm, "end": v(4.12, 44.81) * mm});
            skLineSegment(sketch, "E43", {"start": v(0, 0) * mm, "end": v(5.01, 44.72) * mm});
            skLineSegment(sketch, "E44", {"start": v(4.12, 44.81) * mm, "end": v(5.01, 44.72) * mm});
            skLineSegment(sketch, "E45", {"start": v(0, 0) * mm, "end": v(0, 45) * mm, "construction": true});
            skArc(sketch, "E46.1.0", {"start": v(-3.32, 43.18) * mm, "mid": v(-2.85, 42.77) * mm, "end": v(-2.45, 43.23) * mm});
            skLineSegment(sketch, "E46.1.1", {"start": v(-2.45, 43.23) * mm, "end": v(-2.55, 44.93) * mm});
            skLineSegment(sketch, "E46.1.2", {"start": v(-3.32, 43.18) * mm, "end": v(-3.45, 44.87) * mm});
            skLineSegment(sketch, "E46.1.3", {"start": v(-3.45, 44.87) * mm, "end": v(-2.55, 44.93) * mm});
            skLineSegment(sketch, "E46.1.4", {"start": v(0, 0) * mm, "end": v(-5.04, 44.72) * mm, "construction": true});
            skArc(sketch, "E46.2.0", {"start": v(-8.13, 42.53) * mm, "mid": v(-7.63, 42.18) * mm, "end": v(-7.28, 42.69) * mm});
            skLineSegment(sketch, "E46.2.1", {"start": v(-7.28, 42.69) * mm, "end": v(-7.56, 44.36) * mm});
            skLineSegment(sketch, "E46.2.2", {"start": v(-8.13, 42.53) * mm, "end": v(-8.45, 44.2) * mm});
            skLineSegment(sketch, "E46.2.3", {"start": v(-8.45, 44.2) * mm, "end": v(-7.56, 44.36) * mm});
            skLineSegment(sketch, "E46.2.4", {"start": v(0, 0) * mm, "end": v(-10.01, 43.87) * mm, "construction": true});
            skArc(sketch, "E46.3.0", {"start": v(-12.84, 41.35) * mm, "mid": v(-12.3, 41.06) * mm, "end": v(-12.01, 41.6) * mm});
            skLineSegment(sketch, "E46.3.1", {"start": v(-12.01, 41.6) * mm, "end": v(-12.48, 43.24) * mm});
            skLineSegment(sketch, "E46.3.2", {"start": v(-12.84, 41.35) * mm, "end": v(-13.34, 42.98) * mm});
            skLineSegment(sketch, "E46.3.3", {"start": v(-13.34, 42.98) * mm, "end": v(-12.48, 43.24) * mm});
            skLineSegment(sketch, "E46.3.4", {"start": v(0, 0) * mm, "end": v(-14.86, 42.47) * mm, "construction": true});
            skArc(sketch, "E46.4.0", {"start": v(-17.39, 39.66) * mm, "mid": v(-16.82, 39.43) * mm, "end": v(-16.6, 40) * mm});
            skLineSegment(sketch, "E46.4.1", {"start": v(-16.6, 40) * mm, "end": v(-17.24, 41.57) * mm});
            skLineSegment(sketch, "E46.4.2", {"start": v(-17.39, 39.66) * mm, "end": v(-18.07, 41.21) * mm});
            skLineSegment(sketch, "E46.4.3", {"start": v(-18.07, 41.21) * mm, "end": v(-17.24, 41.57) * mm});
            skLineSegment(sketch, "E46.4.4", {"start": v(0, 0) * mm, "end": v(-19.52, 40.54) * mm, "construction": true});
            skArc(sketch, "E46.5.0", {"start": v(-21.72, 37.46) * mm, "mid": v(-21.13, 37.3) * mm, "end": v(-20.97, 37.89) * mm});
            skLineSegment(sketch, "E46.5.1", {"start": v(-20.97, 37.89) * mm, "end": v(-21.79, 39.38) * mm});
            skLineSegment(sketch, "E46.5.2", {"start": v(-21.72, 37.46) * mm, "end": v(-22.57, 38.93) * mm});
            skLineSegment(sketch, "E46.5.3", {"start": v(-22.57, 38.93) * mm, "end": v(-21.79, 39.38) * mm});
            skLineSegment(sketch, "E46.5.4", {"start": v(0, 0) * mm, "end": v(-23.94, 38.1) * mm, "construction": true});
            skArc(sketch, "E46.6.0", {"start": v(-25.78, 34.8) * mm, "mid": v(-25.17, 34.7) * mm, "end": v(-25.08, 35.3) * mm});
            skLineSegment(sketch, "E46.6.1", {"start": v(-25.08, 35.3) * mm, "end": v(-26.06, 36.69) * mm});
            skLineSegment(sketch, "E46.6.2", {"start": v(-25.78, 34.8) * mm, "end": v(-26.79, 36.16) * mm});
            skLineSegment(sketch, "E46.6.3", {"start": v(-26.79, 36.16) * mm, "end": v(-26.06, 36.69) * mm});
            skLineSegment(sketch, "E46.6.4", {"start": v(0, 0) * mm, "end": v(-28.06, 35.18) * mm, "construction": true});
            skArc(sketch, "E46.7.0", {"start": v(-29.51, 31.69) * mm, "mid": v(-28.9, 31.66) * mm, "end": v(-28.87, 32.27) * mm});
            skLineSegment(sketch, "E46.7.1", {"start": v(-28.87, 32.27) * mm, "end": v(-30, 33.54) * mm});
            skLineSegment(sketch, "E46.7.2", {"start": v(-29.51, 31.69) * mm, "end": v(-30.67, 32.93) * mm});
            skLineSegment(sketch, "E46.7.3", {"start": v(-30.67, 32.93) * mm, "end": v(-30, 33.54) * mm});
            skLineSegment(sketch, "E46.7.4", {"start": v(0, 0) * mm, "end": v(-31.82, 31.82) * mm, "construction": true});
            skArc(sketch, "E46.8.0", {"start": v(-32.87, 28.18) * mm, "mid": v(-32.26, 28.23) * mm, "end": v(-32.3, 28.84) * mm});
            skLineSegment(sketch, "E46.8.1", {"start": v(-32.3, 28.84) * mm, "end": v(-33.57, 29.97) * mm});
            skLineSegment(sketch, "E46.8.2", {"start": v(-32.87, 28.18) * mm, "end": v(-34.16, 29.3) * mm});
            skLineSegment(sketch, "E46.8.3", {"start": v(-34.16, 29.3) * mm, "end": v(-33.57, 29.97) * mm});
            skLineSegment(sketch, "E46.8.4", {"start": v(0, 0) * mm, "end": v(-35.18, 28.06) * mm, "construction": true});
            skArc(sketch, "E46.9.0", {"start": v(-35.82, 24.33) * mm, "mid": v(-35.22, 24.44) * mm, "end": v(-35.33, 25.04) * mm});
            skLineSegment(sketch, "E46.9.1", {"start": v(-35.33, 25.04) * mm, "end": v(-36.72, 26.02) * mm});
            skLineSegment(sketch, "E46.9.2", {"start": v(-35.82, 24.33) * mm, "end": v(-37.23, 25.28) * mm});
            skLineSegment(sketch, "E46.9.3", {"start": v(-37.23, 25.28) * mm, "end": v(-36.72, 26.02) * mm});
            skLineSegment(sketch, "E46.9.4", {"start": v(0, 0) * mm, "end": v(-38.1, 23.94) * mm, "construction": true});
            skArc(sketch, "E46.10.0", {"start": v(-38.32, 20.16) * mm, "mid": v(-37.73, 20.34) * mm, "end": v(-37.91, 20.93) * mm});
            skLineSegment(sketch, "E46.10.1", {"start": v(-37.91, 20.93) * mm, "end": v(-39.4, 21.75) * mm});
            skLineSegment(sketch, "E46.10.2", {"start": v(-38.32, 20.16) * mm, "end": v(-39.83, 20.95) * mm});
            skLineSegment(sketch, "E46.10.3", {"start": v(-39.83, 20.95) * mm, "end": v(-39.4, 21.75) * mm});
            skLineSegment(sketch, "E46.10.4", {"start": v(0, 0) * mm, "end": v(-40.54, 19.52) * mm, "construction": true});
            skArc(sketch, "E46.11.0", {"start": v(-40.34, 15.75) * mm, "mid": v(-39.77, 15.99) * mm, "end": v(-40.01, 16.55) * mm});
            skLineSegment(sketch, "E46.11.1", {"start": v(-40.01, 16.55) * mm, "end": v(-41.59, 17.2) * mm});
            skLineSegment(sketch, "E46.11.2", {"start": v(-40.34, 15.75) * mm, "end": v(-41.92, 16.36) * mm});
            skLineSegment(sketch, "E46.11.3", {"start": v(-41.92, 16.36) * mm, "end": v(-41.59, 17.2) * mm});
            skLineSegment(sketch, "E46.11.4", {"start": v(0, 0) * mm, "end": v(-42.47, 14.86) * mm, "construction": true});
            skArc(sketch, "E46.12.0", {"start": v(-41.85, 11.13) * mm, "mid": v(-41.31, 11.43) * mm, "end": v(-41.62, 11.96) * mm});
            skLineSegment(sketch, "E46.12.1", {"start": v(-41.62, 11.96) * mm, "end": v(-43.25, 12.43) * mm});
            skLineSegment(sketch, "E46.12.2", {"start": v(-41.85, 11.13) * mm, "end": v(-43.5, 11.57) * mm});
            skLineSegment(sketch, "E46.12.3", {"start": v(-43.5, 11.57) * mm, "end": v(-43.25, 12.43) * mm});
            skLineSegment(sketch, "E46.12.4", {"start": v(0, 0) * mm, "end": v(-43.87, 10.01) * mm, "construction": true});
            skArc(sketch, "E46.13.0", {"start": v(-42.83, 6.37) * mm, "mid": v(-42.33, 6.73) * mm, "end": v(-42.7, 7.23) * mm});
            skLineSegment(sketch, "E46.13.1", {"start": v(-42.7, 7.23) * mm, "end": v(-44.37, 7.51) * mm});
            skLineSegment(sketch, "E46.13.2", {"start": v(-42.83, 6.37) * mm, "end": v(-44.51, 6.63) * mm});
            skLineSegment(sketch, "E46.13.3", {"start": v(-44.51, 6.63) * mm, "end": v(-44.37, 7.51) * mm});
            skLineSegment(sketch, "E46.13.4", {"start": v(0, 0) * mm, "end": v(-44.72, 5.04) * mm, "construction": true});
            skArc(sketch, "E46.14.0", {"start": v(-43.27, 1.54) * mm, "mid": v(-42.82, 1.95) * mm, "end": v(-43.24, 2.4) * mm});
            skLineSegment(sketch, "E46.14.1", {"start": v(-43.24, 2.4) * mm, "end": v(-44.93, 2.5) * mm});
            skLineSegment(sketch, "E46.14.2", {"start": v(-43.27, 1.54) * mm, "end": v(-44.97, 1.6) * mm});
            skLineSegment(sketch, "E46.14.3", {"start": v(-44.97, 1.6) * mm, "end": v(-44.93, 2.5) * mm});
            skLineSegment(sketch, "E46.14.4", {"start": v(0, 0) * mm, "end": v(-45, 0) * mm, "construction": true});
            skArc(sketch, "E46.15.0", {"start": v(-43.18, -3.32) * mm, "mid": v(-42.77, -2.85) * mm, "end": v(-43.23, -2.45) * mm});
            skLineSegment(sketch, "E46.15.1", {"start": v(-43.23, -2.45) * mm, "end": v(-44.93, -2.55) * mm});
            skLineSegment(sketch, "E46.15.2", {"start": v(-43.18, -3.32) * mm, "end": v(-44.87, -3.45) * mm});
            skLineSegment(sketch, "E46.15.3", {"start": v(-44.87, -3.45) * mm, "end": v(-44.93, -2.55) * mm});
            skLineSegment(sketch, "E46.15.4", {"start": v(0, 0) * mm, "end": v(-44.72, -5.04) * mm, "construction": true});
            skArc(sketch, "E46.16.0", {"start": v(-42.53, -8.13) * mm, "mid": v(-42.18, -7.63) * mm, "end": v(-42.69, -7.28) * mm});
            skLineSegment(sketch, "E46.16.1", {"start": v(-42.69, -7.28) * mm, "end": v(-44.36, -7.56) * mm});
            skLineSegment(sketch, "E46.16.2", {"start": v(-42.53, -8.13) * mm, "end": v(-44.2, -8.45) * mm});
            skLineSegment(sketch, "E46.16.3", {"start": v(-44.2, -8.45) * mm, "end": v(-44.36, -7.56) * mm});
            skLineSegment(sketch, "E46.16.4", {"start": v(0, 0) * mm, "end": v(-43.87, -10.01) * mm, "construction": true});
            skArc(sketch, "E46.17.0", {"start": v(-41.35, -12.84) * mm, "mid": v(-41.06, -12.3) * mm, "end": v(-41.6, -12.01) * mm});
            skLineSegment(sketch, "E46.17.1", {"start": v(-41.6, -12.01) * mm, "end": v(-43.24, -12.48) * mm});
            skLineSegment(sketch, "E46.17.2", {"start": v(-41.35, -12.84) * mm, "end": v(-42.98, -13.34) * mm});
            skLineSegment(sketch, "E46.17.3", {"start": v(-42.98, -13.34) * mm, "end": v(-43.24, -12.48) * mm});
            skLineSegment(sketch, "E46.17.4", {"start": v(0, 0) * mm, "end": v(-42.47, -14.86) * mm, "construction": true});
            skArc(sketch, "E46.18.0", {"start": v(-39.66, -17.39) * mm, "mid": v(-39.43, -16.82) * mm, "end": v(-40, -16.6) * mm});
            skLineSegment(sketch, "E46.18.1", {"start": v(-40, -16.6) * mm, "end": v(-41.57, -17.24) * mm});
            skLineSegment(sketch, "E46.18.2", {"start": v(-39.66, -17.39) * mm, "end": v(-41.21, -18.07) * mm});
            skLineSegment(sketch, "E46.18.3", {"start": v(-41.21, -18.07) * mm, "end": v(-41.57, -17.24) * mm});
            skLineSegment(sketch, "E46.18.4", {"start": v(0, 0) * mm, "end": v(-40.54, -19.52) * mm, "construction": true});
            skArc(sketch, "E46.19.0", {"start": v(-37.46, -21.72) * mm, "mid": v(-37.3, -21.13) * mm, "end": v(-37.89, -20.97) * mm});
            skLineSegment(sketch, "E46.19.1", {"start": v(-37.89, -20.97) * mm, "end": v(-39.38, -21.79) * mm});
            skLineSegment(sketch, "E46.19.2", {"start": v(-37.46, -21.72) * mm, "end": v(-38.93, -22.57) * mm});
            skLineSegment(sketch, "E46.19.3", {"start": v(-38.93, -22.57) * mm, "end": v(-39.38, -21.79) * mm});
            skLineSegment(sketch, "E46.19.4", {"start": v(0, 0) * mm, "end": v(-38.1, -23.94) * mm, "construction": true});
            skArc(sketch, "E46.20.0", {"start": v(-34.8, -25.78) * mm, "mid": v(-34.7, -25.17) * mm, "end": v(-35.3, -25.08) * mm});
            skLineSegment(sketch, "E46.20.1", {"start": v(-35.3, -25.08) * mm, "end": v(-36.69, -26.06) * mm});
            skLineSegment(sketch, "E46.20.2", {"start": v(-34.8, -25.78) * mm, "end": v(-36.16, -26.79) * mm});
            skLineSegment(sketch, "E46.20.3", {"start": v(-36.16, -26.79) * mm, "end": v(-36.69, -26.06) * mm});
            skLineSegment(sketch, "E46.20.4", {"start": v(0, 0) * mm, "end": v(-35.18, -28.06) * mm, "construction": true});
            skArc(sketch, "E46.21.0", {"start": v(-31.69, -29.51) * mm, "mid": v(-31.66, -28.9) * mm, "end": v(-32.27, -28.87) * mm});
            skLineSegment(sketch, "E46.21.1", {"start": v(-32.27, -28.87) * mm, "end": v(-33.54, -30) * mm});
            skLineSegment(sketch, "E46.21.2", {"start": v(-31.69, -29.51) * mm, "end": v(-32.93, -30.67) * mm});
            skLineSegment(sketch, "E46.21.3", {"start": v(-32.93, -30.67) * mm, "end": v(-33.54, -30) * mm});
            skLineSegment(sketch, "E46.21.4", {"start": v(0, 0) * mm, "end": v(-31.82, -31.82) * mm, "construction": true});
            skArc(sketch, "E46.22.0", {"start": v(-28.18, -32.87) * mm, "mid": v(-28.23, -32.26) * mm, "end": v(-28.84, -32.3) * mm});
            skLineSegment(sketch, "E46.22.1", {"start": v(-28.84, -32.3) * mm, "end": v(-29.97, -33.57) * mm});
            skLineSegment(sketch, "E46.22.2", {"start": v(-28.18, -32.87) * mm, "end": v(-29.3, -34.16) * mm});
            skLineSegment(sketch, "E46.22.3", {"start": v(-29.3, -34.16) * mm, "end": v(-29.97, -33.57) * mm});
            skLineSegment(sketch, "E46.22.4", {"start": v(0, 0) * mm, "end": v(-28.06, -35.18) * mm, "construction": true});
            skArc(sketch, "E46.23.0", {"start": v(-24.33, -35.82) * mm, "mid": v(-24.44, -35.22) * mm, "end": v(-25.04, -35.33) * mm});
            skLineSegment(sketch, "E46.23.1", {"start": v(-25.04, -35.33) * mm, "end": v(-26.02, -36.72) * mm});
            skLineSegment(sketch, "E46.23.2", {"start": v(-24.33, -35.82) * mm, "end": v(-25.28, -37.23) * mm});
            skLineSegment(sketch, "E46.23.3", {"start": v(-25.28, -37.23) * mm, "end": v(-26.02, -36.72) * mm});
            skLineSegment(sketch, "E46.23.4", {"start": v(0, 0) * mm, "end": v(-23.94, -38.1) * mm, "construction": true});
            skArc(sketch, "E46.24.0", {"start": v(-20.16, -38.32) * mm, "mid": v(-20.34, -37.73) * mm, "end": v(-20.93, -37.91) * mm});
            skLineSegment(sketch, "E46.24.1", {"start": v(-20.93, -37.91) * mm, "end": v(-21.75, -39.4) * mm});
            skLineSegment(sketch, "E46.24.2", {"start": v(-20.16, -38.32) * mm, "end": v(-20.95, -39.83) * mm});
            skLineSegment(sketch, "E46.24.3", {"start": v(-20.95, -39.83) * mm, "end": v(-21.75, -39.4) * mm});
            skLineSegment(sketch, "E46.24.4", {"start": v(0, 0) * mm, "end": v(-19.52, -40.54) * mm, "construction": true});
            skArc(sketch, "E46.25.0", {"start": v(-15.75, -40.34) * mm, "mid": v(-15.99, -39.77) * mm, "end": v(-16.55, -40.01) * mm});
            skLineSegment(sketch, "E46.25.1", {"start": v(-16.55, -40.01) * mm, "end": v(-17.2, -41.59) * mm});
            skLineSegment(sketch, "E46.25.2", {"start": v(-15.75, -40.34) * mm, "end": v(-16.36, -41.92) * mm});
            skLineSegment(sketch, "E46.25.3", {"start": v(-16.36, -41.92) * mm, "end": v(-17.2, -41.59) * mm});
            skLineSegment(sketch, "E46.25.4", {"start": v(0, 0) * mm, "end": v(-14.86, -42.47) * mm, "construction": true});
            skArc(sketch, "E46.26.0", {"start": v(-11.13, -41.85) * mm, "mid": v(-11.43, -41.31) * mm, "end": v(-11.96, -41.62) * mm});
            skLineSegment(sketch, "E46.26.1", {"start": v(-11.96, -41.62) * mm, "end": v(-12.43, -43.25) * mm});
            skLineSegment(sketch, "E46.26.2", {"start": v(-11.13, -41.85) * mm, "end": v(-11.57, -43.5) * mm});
            skLineSegment(sketch, "E46.26.3", {"start": v(-11.57, -43.5) * mm, "end": v(-12.43, -43.25) * mm});
            skLineSegment(sketch, "E46.26.4", {"start": v(0, 0) * mm, "end": v(-10.01, -43.87) * mm, "construction": true});
            skArc(sketch, "E46.27.0", {"start": v(-6.37, -42.83) * mm, "mid": v(-6.73, -42.33) * mm, "end": v(-7.23, -42.7) * mm});
            skLineSegment(sketch, "E46.27.1", {"start": v(-7.23, -42.7) * mm, "end": v(-7.51, -44.37) * mm});
            skLineSegment(sketch, "E46.27.2", {"start": v(-6.37, -42.83) * mm, "end": v(-6.63, -44.51) * mm});
            skLineSegment(sketch, "E46.27.3", {"start": v(-6.63, -44.51) * mm, "end": v(-7.51, -44.37) * mm});
            skLineSegment(sketch, "E46.27.4", {"start": v(0, 0) * mm, "end": v(-5.04, -44.72) * mm, "construction": true});
            skArc(sketch, "E46.28.0", {"start": v(-1.54, -43.27) * mm, "mid": v(-1.95, -42.82) * mm, "end": v(-2.4, -43.24) * mm});
            skLineSegment(sketch, "E46.28.1", {"start": v(-2.4, -43.24) * mm, "end": v(-2.5, -44.93) * mm});
            skLineSegment(sketch, "E46.28.2", {"start": v(-1.54, -43.27) * mm, "end": v(-1.6, -44.97) * mm});
            skLineSegment(sketch, "E46.28.3", {"start": v(-1.6, -44.97) * mm, "end": v(-2.5, -44.93) * mm});
            skLineSegment(sketch, "E46.28.4", {"start": v(0, 0) * mm, "end": v(0, -45) * mm, "construction": true});
            skArc(sketch, "E46.29.0", {"start": v(3.32, -43.18) * mm, "mid": v(2.85, -42.77) * mm, "end": v(2.45, -43.23) * mm});
            skLineSegment(sketch, "E46.29.1", {"start": v(2.45, -43.23) * mm, "end": v(2.55, -44.93) * mm});
            skLineSegment(sketch, "E46.29.2", {"start": v(3.32, -43.18) * mm, "end": v(3.45, -44.87) * mm});
            skLineSegment(sketch, "E46.29.3", {"start": v(3.45, -44.87) * mm, "end": v(2.55, -44.93) * mm});
            skLineSegment(sketch, "E46.29.4", {"start": v(0, 0) * mm, "end": v(5.04, -44.72) * mm, "construction": true});
            skArc(sketch, "E46.30.0", {"start": v(8.13, -42.53) * mm, "mid": v(7.63, -42.18) * mm, "end": v(7.28, -42.69) * mm});
            skLineSegment(sketch, "E46.30.1", {"start": v(7.28, -42.69) * mm, "end": v(7.56, -44.36) * mm});
            skLineSegment(sketch, "E46.30.2", {"start": v(8.13, -42.53) * mm, "end": v(8.45, -44.2) * mm});
            skLineSegment(sketch, "E46.30.3", {"start": v(8.45, -44.2) * mm, "end": v(7.56, -44.36) * mm});
            skLineSegment(sketch, "E46.30.4", {"start": v(0, 0) * mm, "end": v(10.01, -43.87) * mm, "construction": true});
            skArc(sketch, "E46.31.0", {"start": v(12.84, -41.35) * mm, "mid": v(12.3, -41.06) * mm, "end": v(12.01, -41.6) * mm});
            skLineSegment(sketch, "E46.31.1", {"start": v(12.01, -41.6) * mm, "end": v(12.48, -43.24) * mm});
            skLineSegment(sketch, "E46.31.2", {"start": v(12.84, -41.35) * mm, "end": v(13.34, -42.98) * mm});
            skLineSegment(sketch, "E46.31.3", {"start": v(13.34, -42.98) * mm, "end": v(12.48, -43.24) * mm});
            skLineSegment(sketch, "E46.31.4", {"start": v(0, 0) * mm, "end": v(14.86, -42.47) * mm, "construction": true});
            skArc(sketch, "E46.32.0", {"start": v(17.39, -39.66) * mm, "mid": v(16.82, -39.43) * mm, "end": v(16.6, -40) * mm});
            skLineSegment(sketch, "E46.32.1", {"start": v(16.6, -40) * mm, "end": v(17.24, -41.57) * mm});
            skLineSegment(sketch, "E46.32.2", {"start": v(17.39, -39.66) * mm, "end": v(18.07, -41.21) * mm});
            skLineSegment(sketch, "E46.32.3", {"start": v(18.07, -41.21) * mm, "end": v(17.24, -41.57) * mm});
            skLineSegment(sketch, "E46.32.4", {"start": v(0, 0) * mm, "end": v(19.52, -40.54) * mm, "construction": true});
            skArc(sketch, "E46.33.0", {"start": v(21.72, -37.46) * mm, "mid": v(21.13, -37.3) * mm, "end": v(20.97, -37.89) * mm});
            skLineSegment(sketch, "E46.33.1", {"start": v(20.97, -37.89) * mm, "end": v(21.79, -39.38) * mm});
            skLineSegment(sketch, "E46.33.2", {"start": v(21.72, -37.46) * mm, "end": v(22.57, -38.93) * mm});
            skLineSegment(sketch, "E46.33.3", {"start": v(22.57, -38.93) * mm, "end": v(21.79, -39.38) * mm});
            skLineSegment(sketch, "E46.33.4", {"start": v(0, 0) * mm, "end": v(23.94, -38.1) * mm, "construction": true});
            skArc(sketch, "E46.34.0", {"start": v(25.78, -34.8) * mm, "mid": v(25.17, -34.7) * mm, "end": v(25.08, -35.3) * mm});
            skLineSegment(sketch, "E46.34.1", {"start": v(25.08, -35.3) * mm, "end": v(26.06, -36.69) * mm});
            skLineSegment(sketch, "E46.34.2", {"start": v(25.78, -34.8) * mm, "end": v(26.79, -36.16) * mm});
            skLineSegment(sketch, "E46.34.3", {"start": v(26.79, -36.16) * mm, "end": v(26.06, -36.69) * mm});
            skLineSegment(sketch, "E46.34.4", {"start": v(0, 0) * mm, "end": v(28.06, -35.18) * mm, "construction": true});
            skArc(sketch, "E46.35.0", {"start": v(29.51, -31.69) * mm, "mid": v(28.9, -31.66) * mm, "end": v(28.87, -32.27) * mm});
            skLineSegment(sketch, "E46.35.1", {"start": v(28.87, -32.27) * mm, "end": v(30, -33.54) * mm});
            skLineSegment(sketch, "E46.35.2", {"start": v(29.51, -31.69) * mm, "end": v(30.67, -32.93) * mm});
            skLineSegment(sketch, "E46.35.3", {"start": v(30.67, -32.93) * mm, "end": v(30, -33.54) * mm});
            skLineSegment(sketch, "E46.35.4", {"start": v(0, 0) * mm, "end": v(31.82, -31.82) * mm, "construction": true});
            skArc(sketch, "E46.36.0", {"start": v(32.87, -28.18) * mm, "mid": v(32.26, -28.23) * mm, "end": v(32.3, -28.84) * mm});
            skLineSegment(sketch, "E46.36.1", {"start": v(32.3, -28.84) * mm, "end": v(33.57, -29.97) * mm});
            skLineSegment(sketch, "E46.36.2", {"start": v(32.87, -28.18) * mm, "end": v(34.16, -29.3) * mm});
            skLineSegment(sketch, "E46.36.3", {"start": v(34.16, -29.3) * mm, "end": v(33.57, -29.97) * mm});
            skLineSegment(sketch, "E46.36.4", {"start": v(0, 0) * mm, "end": v(35.18, -28.06) * mm, "construction": true});
            skArc(sketch, "E46.37.0", {"start": v(35.82, -24.33) * mm, "mid": v(35.22, -24.44) * mm, "end": v(35.33, -25.04) * mm});
            skLineSegment(sketch, "E46.37.1", {"start": v(35.33, -25.04) * mm, "end": v(36.72, -26.02) * mm});
            skLineSegment(sketch, "E46.37.2", {"start": v(35.82, -24.33) * mm, "end": v(37.23, -25.28) * mm});
            skLineSegment(sketch, "E46.37.3", {"start": v(37.23, -25.28) * mm, "end": v(36.72, -26.02) * mm});
            skLineSegment(sketch, "E46.37.4", {"start": v(0, 0) * mm, "end": v(38.1, -23.94) * mm, "construction": true});
            skArc(sketch, "E46.38.0", {"start": v(38.32, -20.16) * mm, "mid": v(37.73, -20.34) * mm, "end": v(37.91, -20.93) * mm});
            skLineSegment(sketch, "E46.38.1", {"start": v(37.91, -20.93) * mm, "end": v(39.4, -21.75) * mm});
            skLineSegment(sketch, "E46.38.2", {"start": v(38.32, -20.16) * mm, "end": v(39.83, -20.95) * mm});
            skLineSegment(sketch, "E46.38.3", {"start": v(39.83, -20.95) * mm, "end": v(39.4, -21.75) * mm});
            skLineSegment(sketch, "E46.38.4", {"start": v(0, 0) * mm, "end": v(40.54, -19.52) * mm, "construction": true});
            skArc(sketch, "E46.39.0", {"start": v(40.34, -15.75) * mm, "mid": v(39.77, -15.99) * mm, "end": v(40.01, -16.55) * mm});
            skLineSegment(sketch, "E46.39.1", {"start": v(40.01, -16.55) * mm, "end": v(41.59, -17.2) * mm});
            skLineSegment(sketch, "E46.39.2", {"start": v(40.34, -15.75) * mm, "end": v(41.92, -16.36) * mm});
            skLineSegment(sketch, "E46.39.3", {"start": v(41.92, -16.36) * mm, "end": v(41.59, -17.2) * mm});
            skLineSegment(sketch, "E46.39.4", {"start": v(0, 0) * mm, "end": v(42.47, -14.86) * mm, "construction": true});
            skArc(sketch, "E46.40.0", {"start": v(41.85, -11.13) * mm, "mid": v(41.31, -11.43) * mm, "end": v(41.62, -11.96) * mm});
            skLineSegment(sketch, "E46.40.1", {"start": v(41.62, -11.96) * mm, "end": v(43.25, -12.43) * mm});
            skLineSegment(sketch, "E46.40.2", {"start": v(41.85, -11.13) * mm, "end": v(43.5, -11.57) * mm});
            skLineSegment(sketch, "E46.40.3", {"start": v(43.5, -11.57) * mm, "end": v(43.25, -12.43) * mm});
            skLineSegment(sketch, "E46.40.4", {"start": v(0, 0) * mm, "end": v(43.87, -10.01) * mm, "construction": true});
            skArc(sketch, "E46.41.0", {"start": v(42.83, -6.37) * mm, "mid": v(42.33, -6.73) * mm, "end": v(42.7, -7.23) * mm});
            skLineSegment(sketch, "E46.41.1", {"start": v(42.7, -7.23) * mm, "end": v(44.37, -7.51) * mm});
            skLineSegment(sketch, "E46.41.2", {"start": v(42.83, -6.37) * mm, "end": v(44.51, -6.63) * mm});
            skLineSegment(sketch, "E46.41.3", {"start": v(44.51, -6.63) * mm, "end": v(44.37, -7.51) * mm});
            skLineSegment(sketch, "E46.41.4", {"start": v(0, 0) * mm, "end": v(44.72, -5.04) * mm, "construction": true});
            skArc(sketch, "E46.42.0", {"start": v(43.27, -1.54) * mm, "mid": v(42.82, -1.95) * mm, "end": v(43.24, -2.4) * mm});
            skLineSegment(sketch, "E46.42.1", {"start": v(43.24, -2.4) * mm, "end": v(44.93, -2.5) * mm});
            skLineSegment(sketch, "E46.42.2", {"start": v(43.27, -1.54) * mm, "end": v(44.97, -1.6) * mm});
            skLineSegment(sketch, "E46.42.3", {"start": v(44.97, -1.6) * mm, "end": v(44.93, -2.5) * mm});
            skLineSegment(sketch, "E46.42.4", {"start": v(0, 0) * mm, "end": v(45, 0) * mm, "construction": true});
            skArc(sketch, "E46.43.0", {"start": v(43.18, 3.32) * mm, "mid": v(42.77, 2.85) * mm, "end": v(43.23, 2.45) * mm});
            skLineSegment(sketch, "E46.43.1", {"start": v(43.23, 2.45) * mm, "end": v(44.93, 2.55) * mm});
            skLineSegment(sketch, "E46.43.2", {"start": v(43.18, 3.32) * mm, "end": v(44.87, 3.45) * mm});
            skLineSegment(sketch, "E46.43.3", {"start": v(44.87, 3.45) * mm, "end": v(44.93, 2.55) * mm});
            skLineSegment(sketch, "E46.43.4", {"start": v(0, 0) * mm, "end": v(44.72, 5.04) * mm, "construction": true});
            skArc(sketch, "E46.44.0", {"start": v(42.53, 8.13) * mm, "mid": v(42.18, 7.63) * mm, "end": v(42.69, 7.28) * mm});
            skLineSegment(sketch, "E46.44.1", {"start": v(42.69, 7.28) * mm, "end": v(44.36, 7.56) * mm});
            skLineSegment(sketch, "E46.44.2", {"start": v(42.53, 8.13) * mm, "end": v(44.2, 8.45) * mm});
            skLineSegment(sketch, "E46.44.3", {"start": v(44.2, 8.45) * mm, "end": v(44.36, 7.56) * mm});
            skLineSegment(sketch, "E46.44.4", {"start": v(0, 0) * mm, "end": v(43.87, 10.01) * mm, "construction": true});
            skArc(sketch, "E46.45.0", {"start": v(41.35, 12.84) * mm, "mid": v(41.06, 12.3) * mm, "end": v(41.6, 12.01) * mm});
            skLineSegment(sketch, "E46.45.1", {"start": v(41.6, 12.01) * mm, "end": v(43.24, 12.48) * mm});
            skLineSegment(sketch, "E46.45.2", {"start": v(41.35, 12.84) * mm, "end": v(42.98, 13.34) * mm});
            skLineSegment(sketch, "E46.45.3", {"start": v(42.98, 13.34) * mm, "end": v(43.24, 12.48) * mm});
            skLineSegment(sketch, "E46.45.4", {"start": v(0, 0) * mm, "end": v(42.47, 14.86) * mm, "construction": true});
            skArc(sketch, "E46.46.0", {"start": v(39.66, 17.39) * mm, "mid": v(39.43, 16.82) * mm, "end": v(40, 16.6) * mm});
            skLineSegment(sketch, "E46.46.1", {"start": v(40, 16.6) * mm, "end": v(41.57, 17.24) * mm});
            skLineSegment(sketch, "E46.46.2", {"start": v(39.66, 17.39) * mm, "end": v(41.21, 18.07) * mm});
            skLineSegment(sketch, "E46.46.3", {"start": v(41.21, 18.07) * mm, "end": v(41.57, 17.24) * mm});
            skLineSegment(sketch, "E46.46.4", {"start": v(0, 0) * mm, "end": v(40.54, 19.52) * mm, "construction": true});
            skArc(sketch, "E46.47.0", {"start": v(37.46, 21.72) * mm, "mid": v(37.3, 21.13) * mm, "end": v(37.89, 20.97) * mm});
            skLineSegment(sketch, "E46.47.1", {"start": v(37.89, 20.97) * mm, "end": v(39.38, 21.79) * mm});
            skLineSegment(sketch, "E46.47.2", {"start": v(37.46, 21.72) * mm, "end": v(38.93, 22.57) * mm});
            skLineSegment(sketch, "E46.47.3", {"start": v(38.93, 22.57) * mm, "end": v(39.38, 21.79) * mm});
            skLineSegment(sketch, "E46.47.4", {"start": v(0, 0) * mm, "end": v(38.1, 23.94) * mm, "construction": true});
            skArc(sketch, "E46.48.0", {"start": v(34.8, 25.78) * mm, "mid": v(34.7, 25.17) * mm, "end": v(35.3, 25.08) * mm});
            skLineSegment(sketch, "E46.48.1", {"start": v(35.3, 25.08) * mm, "end": v(36.69, 26.06) * mm});
            skLineSegment(sketch, "E46.48.2", {"start": v(34.8, 25.78) * mm, "end": v(36.16, 26.79) * mm});
            skLineSegment(sketch, "E46.48.3", {"start": v(36.16, 26.79) * mm, "end": v(36.69, 26.06) * mm});
            skLineSegment(sketch, "E46.48.4", {"start": v(0, 0) * mm, "end": v(35.18, 28.06) * mm, "construction": true});
            skArc(sketch, "E46.49.0", {"start": v(31.69, 29.51) * mm, "mid": v(31.66, 28.9) * mm, "end": v(32.27, 28.87) * mm});
            skLineSegment(sketch, "E46.49.1", {"start": v(32.27, 28.87) * mm, "end": v(33.54, 30) * mm});
            skLineSegment(sketch, "E46.49.2", {"start": v(31.69, 29.51) * mm, "end": v(32.93, 30.67) * mm});
            skLineSegment(sketch, "E46.49.3", {"start": v(32.93, 30.67) * mm, "end": v(33.54, 30) * mm});
            skLineSegment(sketch, "E46.49.4", {"start": v(0, 0) * mm, "end": v(31.82, 31.82) * mm, "construction": true});
            skArc(sketch, "E46.50.0", {"start": v(28.18, 32.87) * mm, "mid": v(28.23, 32.26) * mm, "end": v(28.84, 32.3) * mm});
            skLineSegment(sketch, "E46.50.1", {"start": v(28.84, 32.3) * mm, "end": v(29.97, 33.57) * mm});
            skLineSegment(sketch, "E46.50.2", {"start": v(28.18, 32.87) * mm, "end": v(29.3, 34.16) * mm});
            skLineSegment(sketch, "E46.50.3", {"start": v(29.3, 34.16) * mm, "end": v(29.97, 33.57) * mm});
            skLineSegment(sketch, "E46.50.4", {"start": v(0, 0) * mm, "end": v(28.06, 35.18) * mm, "construction": true});
            skArc(sketch, "E46.51.0", {"start": v(24.33, 35.82) * mm, "mid": v(24.44, 35.22) * mm, "end": v(25.04, 35.33) * mm});
            skLineSegment(sketch, "E46.51.1", {"start": v(25.04, 35.33) * mm, "end": v(26.02, 36.72) * mm});
            skLineSegment(sketch, "E46.51.2", {"start": v(24.33, 35.82) * mm, "end": v(25.28, 37.23) * mm});
            skLineSegment(sketch, "E46.51.3", {"start": v(25.28, 37.23) * mm, "end": v(26.02, 36.72) * mm});
            skLineSegment(sketch, "E46.51.4", {"start": v(0, 0) * mm, "end": v(23.94, 38.1) * mm, "construction": true});
            skArc(sketch, "E46.52.0", {"start": v(20.16, 38.32) * mm, "mid": v(20.34, 37.73) * mm, "end": v(20.93, 37.91) * mm});
            skLineSegment(sketch, "E46.52.1", {"start": v(20.93, 37.91) * mm, "end": v(21.75, 39.4) * mm});
            skLineSegment(sketch, "E46.52.2", {"start": v(20.16, 38.32) * mm, "end": v(20.95, 39.83) * mm});
            skLineSegment(sketch, "E46.52.3", {"start": v(20.95, 39.83) * mm, "end": v(21.75, 39.4) * mm});
            skLineSegment(sketch, "E46.52.4", {"start": v(0, 0) * mm, "end": v(19.52, 40.54) * mm, "construction": true});
            skArc(sketch, "E46.53.0", {"start": v(15.75, 40.34) * mm, "mid": v(15.99, 39.77) * mm, "end": v(16.55, 40.01) * mm});
            skLineSegment(sketch, "E46.53.1", {"start": v(16.55, 40.01) * mm, "end": v(17.2, 41.59) * mm});
            skLineSegment(sketch, "E46.53.2", {"start": v(15.75, 40.34) * mm, "end": v(16.36, 41.92) * mm});
            skLineSegment(sketch, "E46.53.3", {"start": v(16.36, 41.92) * mm, "end": v(17.2, 41.59) * mm});
            skLineSegment(sketch, "E46.53.4", {"start": v(0, 0) * mm, "end": v(14.86, 42.47) * mm, "construction": true});
            skArc(sketch, "E46.54.0", {"start": v(11.13, 41.85) * mm, "mid": v(11.43, 41.31) * mm, "end": v(11.96, 41.62) * mm});
            skLineSegment(sketch, "E46.54.1", {"start": v(11.96, 41.62) * mm, "end": v(12.43, 43.25) * mm});
            skLineSegment(sketch, "E46.54.2", {"start": v(11.13, 41.85) * mm, "end": v(11.57, 43.5) * mm});
            skLineSegment(sketch, "E46.54.3", {"start": v(11.57, 43.5) * mm, "end": v(12.43, 43.25) * mm});
            skLineSegment(sketch, "E46.54.4", {"start": v(0, 0) * mm, "end": v(10.01, 43.87) * mm, "construction": true});
            skArc(sketch, "E46.55.0", {"start": v(6.37, 42.83) * mm, "mid": v(6.73, 42.33) * mm, "end": v(7.23, 42.7) * mm});
            skLineSegment(sketch, "E46.55.1", {"start": v(7.23, 42.7) * mm, "end": v(7.51, 44.37) * mm});
            skLineSegment(sketch, "E46.55.2", {"start": v(6.37, 42.83) * mm, "end": v(6.63, 44.51) * mm});
            skLineSegment(sketch, "E46.55.3", {"start": v(6.63, 44.51) * mm, "end": v(7.51, 44.37) * mm});
            skPoint(sketch, "E46.center", {"position": v(0, 0) * mm});
            skLineSegment(sketch, "E47.1.0", {"start": v(0, 0) * mm, "end": v(-0.02, 45) * mm});
            skLineSegment(sketch, "E47.1.1", {"start": v(0, 0) * mm, "end": v(-0.92, 45) * mm});
            skLineSegment(sketch, "E47.1.2", {"start": v(-0.92, 45) * mm, "end": v(-0.02, 45) * mm});
            skLineSegment(sketch, "E47.2.0", {"start": v(0, 0) * mm, "end": v(-5.06, 44.72) * mm});
            skLineSegment(sketch, "E47.2.1", {"start": v(0, 0) * mm, "end": v(-5.96, 44.6) * mm});
            skLineSegment(sketch, "E47.2.2", {"start": v(-5.96, 44.6) * mm, "end": v(-5.06, 44.72) * mm});
            skLineSegment(sketch, "E47.3.0", {"start": v(0, 0) * mm, "end": v(-10.04, 43.87) * mm});
            skLineSegment(sketch, "E47.3.1", {"start": v(0, 0) * mm, "end": v(-10.91, 43.66) * mm});
            skLineSegment(sketch, "E47.3.2", {"start": v(-10.91, 43.66) * mm, "end": v(-10.04, 43.87) * mm});
            skLineSegment(sketch, "E47.4.0", {"start": v(0, 0) * mm, "end": v(-14.89, 42.47) * mm});
            skLineSegment(sketch, "E47.4.1", {"start": v(0, 0) * mm, "end": v(-15.73, 42.16) * mm});
            skLineSegment(sketch, "E47.4.2", {"start": v(-15.73, 42.16) * mm, "end": v(-14.89, 42.47) * mm});
            skLineSegment(sketch, "E47.5.0", {"start": v(0, 0) * mm, "end": v(-19.55, 40.53) * mm});
            skLineSegment(sketch, "E47.5.1", {"start": v(0, 0) * mm, "end": v(-20.35, 40.14) * mm});
            skLineSegment(sketch, "E47.5.2", {"start": v(-20.35, 40.14) * mm, "end": v(-19.55, 40.53) * mm});
            skLineSegment(sketch, "E47.6.0", {"start": v(0, 0) * mm, "end": v(-23.96, 38.1) * mm});
            skLineSegment(sketch, "E47.6.1", {"start": v(0, 0) * mm, "end": v(-24.72, 37.6) * mm});
            skLineSegment(sketch, "E47.6.2", {"start": v(-24.72, 37.6) * mm, "end": v(-23.96, 38.1) * mm});
            skLineSegment(sketch, "E47.7.0", {"start": v(0, 0) * mm, "end": v(-28.08, 35.17) * mm});
            skLineSegment(sketch, "E47.7.1", {"start": v(0, 0) * mm, "end": v(-28.78, 34.6) * mm});
            skLineSegment(sketch, "E47.7.2", {"start": v(-28.78, 34.6) * mm, "end": v(-28.08, 35.17) * mm});
            skLineSegment(sketch, "E47.8.0", {"start": v(0, 0) * mm, "end": v(-31.84, 31.8) * mm});
            skLineSegment(sketch, "E47.8.1", {"start": v(0, 0) * mm, "end": v(-32.47, 31.16) * mm});
            skLineSegment(sketch, "E47.8.2", {"start": v(-32.47, 31.16) * mm, "end": v(-31.84, 31.8) * mm});
            skLineSegment(sketch, "E47.9.0", {"start": v(0, 0) * mm, "end": v(-35.2, 28.04) * mm});
            skLineSegment(sketch, "E47.9.1", {"start": v(0, 0) * mm, "end": v(-35.75, 27.33) * mm});
            skLineSegment(sketch, "E47.9.2", {"start": v(-35.75, 27.33) * mm, "end": v(-35.2, 28.04) * mm});
            skLineSegment(sketch, "E47.10.0", {"start": v(0, 0) * mm, "end": v(-38.12, 23.92) * mm});
            skLineSegment(sketch, "E47.10.1", {"start": v(0, 0) * mm, "end": v(-38.59, 23.15) * mm});
            skLineSegment(sketch, "E47.10.2", {"start": v(-38.59, 23.15) * mm, "end": v(-38.12, 23.92) * mm});
            skLineSegment(sketch, "E47.11.0", {"start": v(0, 0) * mm, "end": v(-40.56, 19.5) * mm});
            skLineSegment(sketch, "E47.11.1", {"start": v(0, 0) * mm, "end": v(-40.94, 18.69) * mm});
            skLineSegment(sketch, "E47.11.2", {"start": v(-40.94, 18.69) * mm, "end": v(-40.56, 19.5) * mm});
            skLineSegment(sketch, "E47.12.0", {"start": v(0, 0) * mm, "end": v(-42.48, 14.84) * mm});
            skLineSegment(sketch, "E47.12.1", {"start": v(0, 0) * mm, "end": v(-42.77, 13.99) * mm});
            skLineSegment(sketch, "E47.12.2", {"start": v(-42.77, 13.99) * mm, "end": v(-42.48, 14.84) * mm});
            skLineSegment(sketch, "E47.13.0", {"start": v(0, 0) * mm, "end": v(-43.88, 10) * mm});
            skLineSegment(sketch, "E47.13.1", {"start": v(0, 0) * mm, "end": v(-44.07, 9.11) * mm});
            skLineSegment(sketch, "E47.13.2", {"start": v(-44.07, 9.11) * mm, "end": v(-43.88, 10) * mm});
            skLineSegment(sketch, "E47.14.0", {"start": v(0, 0) * mm, "end": v(-44.72, 5.01) * mm});
            skLineSegment(sketch, "E47.14.1", {"start": v(0, 0) * mm, "end": v(-44.81, 4.12) * mm});
            skLineSegment(sketch, "E47.14.2", {"start": v(-44.81, 4.12) * mm, "end": v(-44.72, 5.01) * mm});
            skLineSegment(sketch, "E47.15.0", {"start": v(0, 0) * mm, "end": v(-45, -0.02) * mm});
            skLineSegment(sketch, "E47.15.1", {"start": v(0, 0) * mm, "end": v(-45, -0.92) * mm});
            skLineSegment(sketch, "E47.15.2", {"start": v(-45, -0.92) * mm, "end": v(-45, -0.02) * mm});
            skLineSegment(sketch, "E47.16.0", {"start": v(0, 0) * mm, "end": v(-44.72, -5.06) * mm});
            skLineSegment(sketch, "E47.16.1", {"start": v(0, 0) * mm, "end": v(-44.6, -5.96) * mm});
            skLineSegment(sketch, "E47.16.2", {"start": v(-44.6, -5.96) * mm, "end": v(-44.72, -5.06) * mm});
            skLineSegment(sketch, "E47.17.0", {"start": v(0, 0) * mm, "end": v(-43.87, -10.04) * mm});
            skLineSegment(sketch, "E47.17.1", {"start": v(0, 0) * mm, "end": v(-43.66, -10.91) * mm});
            skLineSegment(sketch, "E47.17.2", {"start": v(-43.66, -10.91) * mm, "end": v(-43.87, -10.04) * mm});
            skLineSegment(sketch, "E47.18.0", {"start": v(0, 0) * mm, "end": v(-42.47, -14.89) * mm});
            skLineSegment(sketch, "E47.18.1", {"start": v(0, 0) * mm, "end": v(-42.16, -15.73) * mm});
            skLineSegment(sketch, "E47.18.2", {"start": v(-42.16, -15.73) * mm, "end": v(-42.47, -14.89) * mm});
            skLineSegment(sketch, "E47.19.0", {"start": v(0, 0) * mm, "end": v(-40.53, -19.55) * mm});
            skLineSegment(sketch, "E47.19.1", {"start": v(0, 0) * mm, "end": v(-40.14, -20.35) * mm});
            skLineSegment(sketch, "E47.19.2", {"start": v(-40.14, -20.35) * mm, "end": v(-40.53, -19.55) * mm});
            skLineSegment(sketch, "E47.20.0", {"start": v(0, 0) * mm, "end": v(-38.1, -23.96) * mm});
            skLineSegment(sketch, "E47.20.1", {"start": v(0, 0) * mm, "end": v(-37.6, -24.72) * mm});
            skLineSegment(sketch, "E47.20.2", {"start": v(-37.6, -24.72) * mm, "end": v(-38.1, -23.96) * mm});
            skLineSegment(sketch, "E47.21.0", {"start": v(0, 0) * mm, "end": v(-35.17, -28.08) * mm});
            skLineSegment(sketch, "E47.21.1", {"start": v(0, 0) * mm, "end": v(-34.6, -28.78) * mm});
            skLineSegment(sketch, "E47.21.2", {"start": v(-34.6, -28.78) * mm, "end": v(-35.17, -28.08) * mm});
            skLineSegment(sketch, "E47.22.0", {"start": v(0, 0) * mm, "end": v(-31.8, -31.84) * mm});
            skLineSegment(sketch, "E47.22.1", {"start": v(0, 0) * mm, "end": v(-31.16, -32.47) * mm});
            skLineSegment(sketch, "E47.22.2", {"start": v(-31.16, -32.47) * mm, "end": v(-31.8, -31.84) * mm});
            skLineSegment(sketch, "E47.23.0", {"start": v(0, 0) * mm, "end": v(-28.04, -35.2) * mm});
            skLineSegment(sketch, "E47.23.1", {"start": v(0, 0) * mm, "end": v(-27.33, -35.75) * mm});
            skLineSegment(sketch, "E47.23.2", {"start": v(-27.33, -35.75) * mm, "end": v(-28.04, -35.2) * mm});
            skLineSegment(sketch, "E47.24.0", {"start": v(0, 0) * mm, "end": v(-23.92, -38.12) * mm});
            skLineSegment(sketch, "E47.24.1", {"start": v(0, 0) * mm, "end": v(-23.15, -38.59) * mm});
            skLineSegment(sketch, "E47.24.2", {"start": v(-23.15, -38.59) * mm, "end": v(-23.92, -38.12) * mm});
            skLineSegment(sketch, "E47.25.0", {"start": v(0, 0) * mm, "end": v(-19.5, -40.56) * mm});
            skLineSegment(sketch, "E47.25.1", {"start": v(0, 0) * mm, "end": v(-18.69, -40.94) * mm});
            skLineSegment(sketch, "E47.25.2", {"start": v(-18.69, -40.94) * mm, "end": v(-19.5, -40.56) * mm});
            skLineSegment(sketch, "E47.26.0", {"start": v(0, 0) * mm, "end": v(-14.84, -42.48) * mm});
            skLineSegment(sketch, "E47.26.1", {"start": v(0, 0) * mm, "end": v(-13.99, -42.77) * mm});
            skLineSegment(sketch, "E47.26.2", {"start": v(-13.99, -42.77) * mm, "end": v(-14.84, -42.48) * mm});
            skLineSegment(sketch, "E47.27.0", {"start": v(0, 0) * mm, "end": v(-10, -43.88) * mm});
            skLineSegment(sketch, "E47.27.1", {"start": v(0, 0) * mm, "end": v(-9.11, -44.07) * mm});
            skLineSegment(sketch, "E47.27.2", {"start": v(-9.11, -44.07) * mm, "end": v(-10, -43.88) * mm});
            skLineSegment(sketch, "E47.28.0", {"start": v(0, 0) * mm, "end": v(-5.01, -44.72) * mm});
            skLineSegment(sketch, "E47.28.1", {"start": v(0, 0) * mm, "end": v(-4.12, -44.81) * mm});
            skLineSegment(sketch, "E47.28.2", {"start": v(-4.12, -44.81) * mm, "end": v(-5.01, -44.72) * mm});
            skLineSegment(sketch, "E47.29.0", {"start": v(0, 0) * mm, "end": v(0.02, -45) * mm});
            skLineSegment(sketch, "E47.29.1", {"start": v(0, 0) * mm, "end": v(0.92, -45) * mm});
            skLineSegment(sketch, "E47.29.2", {"start": v(0.92, -45) * mm, "end": v(0.02, -45) * mm});
            skLineSegment(sketch, "E47.30.0", {"start": v(0, 0) * mm, "end": v(5.06, -44.72) * mm});
            skLineSegment(sketch, "E47.30.1", {"start": v(0, 0) * mm, "end": v(5.96, -44.6) * mm});
            skLineSegment(sketch, "E47.30.2", {"start": v(5.96, -44.6) * mm, "end": v(5.06, -44.72) * mm});
            skLineSegment(sketch, "E47.31.0", {"start": v(0, 0) * mm, "end": v(10.04, -43.87) * mm});
            skLineSegment(sketch, "E47.31.1", {"start": v(0, 0) * mm, "end": v(10.91, -43.66) * mm});
            skLineSegment(sketch, "E47.31.2", {"start": v(10.91, -43.66) * mm, "end": v(10.04, -43.87) * mm});
            skLineSegment(sketch, "E47.32.0", {"start": v(0, 0) * mm, "end": v(14.89, -42.47) * mm});
            skLineSegment(sketch, "E47.32.1", {"start": v(0, 0) * mm, "end": v(15.73, -42.16) * mm});
            skLineSegment(sketch, "E47.32.2", {"start": v(15.73, -42.16) * mm, "end": v(14.89, -42.47) * mm});
            skLineSegment(sketch, "E47.33.0", {"start": v(0, 0) * mm, "end": v(19.55, -40.53) * mm});
            skLineSegment(sketch, "E47.33.1", {"start": v(0, 0) * mm, "end": v(20.35, -40.14) * mm});
            skLineSegment(sketch, "E47.33.2", {"start": v(20.35, -40.14) * mm, "end": v(19.55, -40.53) * mm});
            skLineSegment(sketch, "E47.34.0", {"start": v(0, 0) * mm, "end": v(23.96, -38.1) * mm});
            skLineSegment(sketch, "E47.34.1", {"start": v(0, 0) * mm, "end": v(24.72, -37.6) * mm});
            skLineSegment(sketch, "E47.34.2", {"start": v(24.72, -37.6) * mm, "end": v(23.96, -38.1) * mm});
            skLineSegment(sketch, "E47.35.0", {"start": v(0, 0) * mm, "end": v(28.08, -35.17) * mm});
            skLineSegment(sketch, "E47.35.1", {"start": v(0, 0) * mm, "end": v(28.78, -34.6) * mm});
            skLineSegment(sketch, "E47.35.2", {"start": v(28.78, -34.6) * mm, "end": v(28.08, -35.17) * mm});
            skLineSegment(sketch, "E47.36.0", {"start": v(0, 0) * mm, "end": v(31.84, -31.8) * mm});
            skLineSegment(sketch, "E47.36.1", {"start": v(0, 0) * mm, "end": v(32.47, -31.16) * mm});
            skLineSegment(sketch, "E47.36.2", {"start": v(32.47, -31.16) * mm, "end": v(31.84, -31.8) * mm});
            skLineSegment(sketch, "E47.37.0", {"start": v(0, 0) * mm, "end": v(35.2, -28.04) * mm});
            skLineSegment(sketch, "E47.37.1", {"start": v(0, 0) * mm, "end": v(35.75, -27.33) * mm});
            skLineSegment(sketch, "E47.37.2", {"start": v(35.75, -27.33) * mm, "end": v(35.2, -28.04) * mm});
            skLineSegment(sketch, "E47.38.0", {"start": v(0, 0) * mm, "end": v(38.12, -23.92) * mm});
            skLineSegment(sketch, "E47.38.1", {"start": v(0, 0) * mm, "end": v(38.59, -23.15) * mm});
            skLineSegment(sketch, "E47.38.2", {"start": v(38.59, -23.15) * mm, "end": v(38.12, -23.92) * mm});
            skLineSegment(sketch, "E47.39.0", {"start": v(0, 0) * mm, "end": v(40.56, -19.5) * mm});
            skLineSegment(sketch, "E47.39.1", {"start": v(0, 0) * mm, "end": v(40.94, -18.69) * mm});
            skLineSegment(sketch, "E47.39.2", {"start": v(40.94, -18.69) * mm, "end": v(40.56, -19.5) * mm});
            skLineSegment(sketch, "E47.40.0", {"start": v(0, 0) * mm, "end": v(42.48, -14.84) * mm});
            skLineSegment(sketch, "E47.40.1", {"start": v(0, 0) * mm, "end": v(42.77, -13.99) * mm});
            skLineSegment(sketch, "E47.40.2", {"start": v(42.77, -13.99) * mm, "end": v(42.48, -14.84) * mm});
            skLineSegment(sketch, "E47.41.0", {"start": v(0, 0) * mm, "end": v(43.88, -10) * mm});
            skLineSegment(sketch, "E47.41.1", {"start": v(0, 0) * mm, "end": v(44.07, -9.11) * mm});
            skLineSegment(sketch, "E47.41.2", {"start": v(44.07, -9.11) * mm, "end": v(43.88, -10) * mm});
            skLineSegment(sketch, "E47.42.0", {"start": v(0, 0) * mm, "end": v(44.72, -5.01) * mm});
            skLineSegment(sketch, "E47.42.1", {"start": v(0, 0) * mm, "end": v(44.81, -4.12) * mm});
            skLineSegment(sketch, "E47.42.2", {"start": v(44.81, -4.12) * mm, "end": v(44.72, -5.01) * mm});
            skLineSegment(sketch, "E47.43.0", {"start": v(0, 0) * mm, "end": v(45, 0.02) * mm});
            skLineSegment(sketch, "E47.43.1", {"start": v(0, 0) * mm, "end": v(45, 0.92) * mm});
            skLineSegment(sketch, "E47.43.2", {"start": v(45, 0.92) * mm, "end": v(45, 0.02) * mm});
            skLineSegment(sketch, "E47.44.0", {"start": v(0, 0) * mm, "end": v(44.72, 5.06) * mm});
            skLineSegment(sketch, "E47.44.1", {"start": v(0, 0) * mm, "end": v(44.6, 5.96) * mm});
            skLineSegment(sketch, "E47.44.2", {"start": v(44.6, 5.96) * mm, "end": v(44.72, 5.06) * mm});
            skLineSegment(sketch, "E47.45.0", {"start": v(0, 0) * mm, "end": v(43.87, 10.04) * mm});
            skLineSegment(sketch, "E47.45.1", {"start": v(0, 0) * mm, "end": v(43.66, 10.91) * mm});
            skLineSegment(sketch, "E47.45.2", {"start": v(43.66, 10.91) * mm, "end": v(43.87, 10.04) * mm});
            skLineSegment(sketch, "E47.46.0", {"start": v(0, 0) * mm, "end": v(42.47, 14.89) * mm});
            skLineSegment(sketch, "E47.46.1", {"start": v(0, 0) * mm, "end": v(42.16, 15.73) * mm});
            skLineSegment(sketch, "E47.46.2", {"start": v(42.16, 15.73) * mm, "end": v(42.47, 14.89) * mm});
            skLineSegment(sketch, "E47.47.0", {"start": v(0, 0) * mm, "end": v(40.53, 19.55) * mm});
            skLineSegment(sketch, "E47.47.1", {"start": v(0, 0) * mm, "end": v(40.14, 20.35) * mm});
            skLineSegment(sketch, "E47.47.2", {"start": v(40.14, 20.35) * mm, "end": v(40.53, 19.55) * mm});
            skLineSegment(sketch, "E47.48.0", {"start": v(0, 0) * mm, "end": v(38.1, 23.96) * mm});
            skLineSegment(sketch, "E47.48.1", {"start": v(0, 0) * mm, "end": v(37.6, 24.72) * mm});
            skLineSegment(sketch, "E47.48.2", {"start": v(37.6, 24.72) * mm, "end": v(38.1, 23.96) * mm});
            skLineSegment(sketch, "E47.49.0", {"start": v(0, 0) * mm, "end": v(35.17, 28.08) * mm});
            skLineSegment(sketch, "E47.49.1", {"start": v(0, 0) * mm, "end": v(34.6, 28.78) * mm});
            skLineSegment(sketch, "E47.49.2", {"start": v(34.6, 28.78) * mm, "end": v(35.17, 28.08) * mm});
            skLineSegment(sketch, "E47.50.0", {"start": v(0, 0) * mm, "end": v(31.8, 31.84) * mm});
            skLineSegment(sketch, "E47.50.1", {"start": v(0, 0) * mm, "end": v(31.16, 32.47) * mm});
            skLineSegment(sketch, "E47.50.2", {"start": v(31.16, 32.47) * mm, "end": v(31.8, 31.84) * mm});
            skLineSegment(sketch, "E47.51.0", {"start": v(0, 0) * mm, "end": v(28.04, 35.2) * mm});
            skLineSegment(sketch, "E47.51.1", {"start": v(0, 0) * mm, "end": v(27.33, 35.75) * mm});
            skLineSegment(sketch, "E47.51.2", {"start": v(27.33, 35.75) * mm, "end": v(28.04, 35.2) * mm});
            skLineSegment(sketch, "E47.52.0", {"start": v(0, 0) * mm, "end": v(23.92, 38.12) * mm});
            skLineSegment(sketch, "E47.52.1", {"start": v(0, 0) * mm, "end": v(23.15, 38.59) * mm});
            skLineSegment(sketch, "E47.52.2", {"start": v(23.15, 38.59) * mm, "end": v(23.92, 38.12) * mm});
            skLineSegment(sketch, "E47.53.0", {"start": v(0, 0) * mm, "end": v(19.5, 40.56) * mm});
            skLineSegment(sketch, "E47.53.1", {"start": v(0, 0) * mm, "end": v(18.69, 40.94) * mm});
            skLineSegment(sketch, "E47.53.2", {"start": v(18.69, 40.94) * mm, "end": v(19.5, 40.56) * mm});
            skLineSegment(sketch, "E47.54.0", {"start": v(0, 0) * mm, "end": v(14.84, 42.48) * mm});
            skLineSegment(sketch, "E47.54.1", {"start": v(0, 0) * mm, "end": v(13.99, 42.77) * mm});
            skLineSegment(sketch, "E47.54.2", {"start": v(13.99, 42.77) * mm, "end": v(14.84, 42.48) * mm});
            skLineSegment(sketch, "E47.55.0", {"start": v(0, 0) * mm, "end": v(10, 43.88) * mm});
            skLineSegment(sketch, "E47.55.1", {"start": v(0, 0) * mm, "end": v(9.11, 44.07) * mm});
            skLineSegment(sketch, "E47.55.2", {"start": v(9.11, 44.07) * mm, "end": v(10, 43.88) * mm});
            skSolve(sketch);
        }
        {
            var Q0;
            Q0 = qSketchRegion(id + "F4", true);
            extrude(context, id + "F5", {"entities" : qUnion([Q0]), "operationType" : NewBodyOperationType.REMOVE, "endBound" : BoundingType.THROUGH_ALL, "depth" : 25 * mm, "offsetDistance" : 25 * mm});
        }
    });
